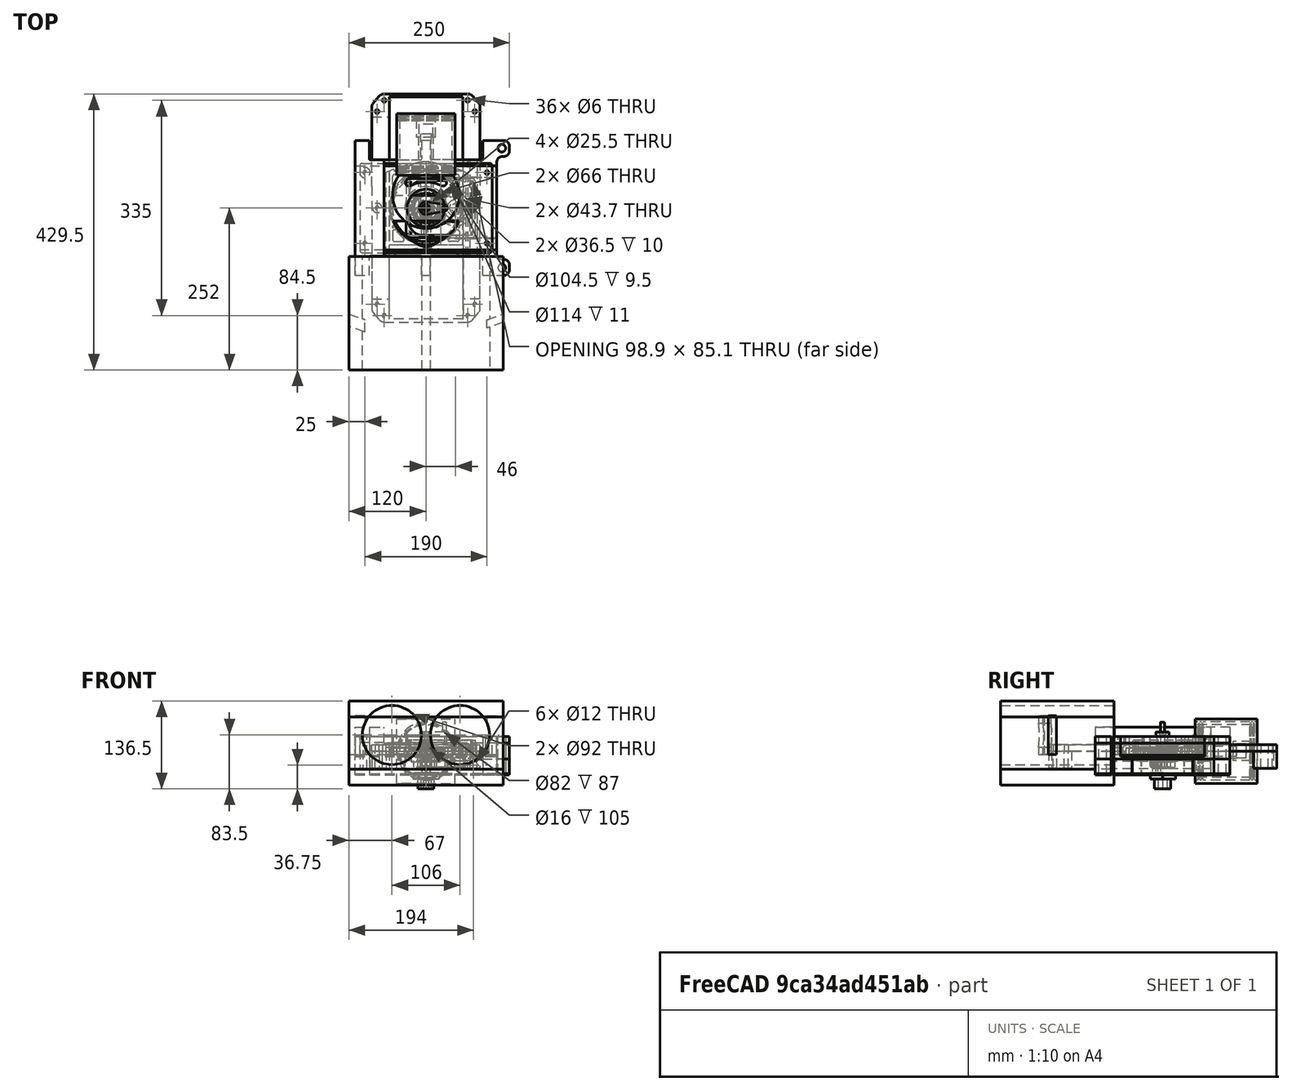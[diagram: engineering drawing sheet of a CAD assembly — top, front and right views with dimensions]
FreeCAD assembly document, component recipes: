
FREECAD ASSEMBLY — COMPONENT RECIPES ("assm4_Paired_at_Tusi_engine")

This assembly document has 39 components, labeled P0..P38 below (a component is one placed body or linked part). 38 of them carry a construction recipe — the FreeCAD feature program that regenerates the part from scratch, quoted from this document or its linked companion documents; the rest are supplied as boundary geometry only. No exploded tour is included for this assembly.
NOTE — this tour is split across 2 documents so each fits a 32k-token context. This is document 1: the component sections continue in the remaining 1 document, each repeating the header above.
COMPONENT P0 — geometry summary ("Assembly_total"; no construction recipe available for this part):
  bounding box: 108.1 x 92.0 x 62.2 mm
  tessellated surface: 9,740 triangles
  volume: 74990775681339383338264170385400035557474644223494673803599843481863248417572032395124455590544277504 mm^3 (12113090433333364260136632761595625055943688050167025185754855824423538995780718082348980511965184% of its bounding box)
  symmetry: mirror-symmetric across its x mid-plane
COMPONENT P1 — recipe-attached ("Шток_поршня", modeled in this document).
Construction recipe (the document's own serialized feature program — sketch geometry with constraints, then the solid features built on it; lengths are millimeters unless a unit is written):

FEATURE [PartDesign::CoordinateSystem] Pin
  AttacherType = Attacher::AttachEngine3D
  MapMode = 45
  Placement = pos=(5.1e-14,85,0) rot=(0.57735,0.57735,0.57735;2.0944rad)
FEATURE [Sketcher::SketchObject] Sketch053
  FullyConstrained = true
  MapMode = 5
  Placement = pos=(0,0,0) rot=(1,0,0;1.5708rad)
  Support = -> [XZ_Plane001]
  sketch-geometry (2):
    g0: Circle CenterX=0 CenterY=0 CenterZ=0 NormalX=0 NormalY=0 NormalZ=1 AngleXU=0 Radius=11
    g1: Circle CenterX=0 CenterY=0 CenterZ=0 NormalX=0 NormalY=0 NormalZ=1 AngleXU=0 Radius=8
  constraints (4):
    c: Coincident(g0,g-1)
    c: Coincident(g1,g0)
    c: Diameter(g0) = 22
    c: Diameter(g1) = 16
FEATURE [PartDesign::Pad] Pad
  Direction = (0,-1,-2e-16)
  Length = 115
  Length2 = 7.5
  Placement = pos=(0,0,0) rot=(1,0,0;1.5708rad)
  Profile = -> Sketch053
  ReferenceAxis = -> Sketch053 [N_Axis]
  Reversed = true
  Type = 4
FEATURE [Sketcher::SketchObject] Sketch054
  FullyConstrained = true
  MapMode = 5
  Placement = pos=(0,0,0) rot=(1,0,0;1.5708rad)
  Support = -> [XZ_Plane001]
  sketch-geometry (2):
    g0: Circle CenterX=0 CenterY=0 CenterZ=0 NormalX=0 NormalY=0 NormalZ=1 AngleXU=0 Radius=11
    g1: Circle CenterX=0 CenterY=0 CenterZ=0 NormalX=0 NormalY=0 NormalZ=1 AngleXU=0 Radius=3
  constraints (4):
    c: Coincident(g0,g-1)
    c: Diameter(g0) = 22
    c: Coincident(g1,g0)
    c: Diameter(g1) = 6
FEATURE [PartDesign::Pad] Pad025
  BaseFeature = -> Pad
  Direction = (0,-1,-2e-16)
  Length = 10
  Length2 = 10
  Placement = pos=(0,0,0) rot=(1,0,0;1.5708rad)
  Profile = -> Sketch054
  ReferenceAxis = -> Sketch054 [N_Axis]
  Reversed = true
  Type = 0
FEATURE [Sketcher::SketchObject] Sketch055
  ExternalGeometry = -> [Pad025]
  FullyConstrained = true
  MapMode = 5
  Placement = pos=(0,0,0) rot=(1,0,0;1.5708rad)
  Support = -> [XZ_Plane001]
  sketch-geometry (2):
    g0: Circle CenterX=0 CenterY=0 CenterZ=0 NormalX=0 NormalY=0 NormalZ=1 AngleXU=0 Radius=7
    g1: Circle CenterX=0 CenterY=0 CenterZ=0 NormalX=0 NormalY=0 NormalZ=1 AngleXU=0 Radius=3
  constraints (4):
    c: Coincident(g0,g-3)
    c: Diameter(g0) = 14
    c: Coincident(g1,g0)
    c: Equal(g-3,g1)
FEATURE [PartDesign::Pad] Pad026
  BaseFeature = -> Pad025
  Direction = (0,-1,-2e-16)
  Length = 45
  Length2 = 10
  Placement = pos=(0,0,0) rot=(1,0,0;1.5708rad)
  Profile = -> Sketch055
  ReferenceAxis = -> Sketch055 [N_Axis]
  Type = 0
FEATURE [PartDesign::Body] Body  label="Шток_поршня"
  Group = -> [Pin,Sketch053,Pad,Sketch054,Pad025,Sketch055,Pad026]
  Origin = -> Origin001
  Tip = -> Pad026
COMPONENT P2 — recipe-attached ("Эксцентрик", modeled in this document).
Construction recipe (the document's own serialized feature program — sketch geometry with constraints, then the solid features built on it; lengths are millimeters unless a unit is written):

FEATURE [Sketcher::SketchObject] Sketch005
  FullyConstrained = true
  MapMode = 5
  Support = -> [XY_Plane002]
  expr: Constraints[1] = <<Dim_table>>.crank_dia2 + <<Dim_table>>.zazor
  expr: Constraints[26] = <<Dim_table>>.crank_dia2 * 0.4
  expr: Constraints[27] = <<Dim_table>>.ecc_dia * 0.8
  expr: Constraints[29] = <<Dim_table>>.crank_dia2 * 1.5
  expr: Constraints[2] = <<Dim_table>>.ecc_dia
  expr: Constraints[3] = <<Dim_table>>.crank_len
  sketch-geometry (14):
    g0: Circle CenterX=0 CenterY=-9.5 CenterZ=0 NormalX=0 NormalY=0 NormalZ=1 AngleXU=0 Radius=18
    g1: Circle CenterX=0 CenterY=0 CenterZ=0 NormalX=0 NormalY=0 NormalZ=1 AngleXU=0 Radius=6.5
    g2: ArcOfCircle CenterX=0 CenterY=-9.5 CenterZ=0 NormalX=0 NormalY=0 NormalZ=1 AngleXU=0 Radius=14.4 StartAngle=2.38131 EndAngle=4.4845
    g3: ArcOfCircle CenterX=0 CenterY=-9.5 CenterZ=0 NormalX=0 NormalY=0 NormalZ=1 AngleXU=0 Radius=14.4 StartAngle=4.94028 EndAngle=7.04347
    g4: LineSegment StartX=-2.5 StartY=-9.49157 StartZ=0 EndX=-2.5 EndY=-22.9291 EndZ=0
    g5: LineSegment StartX=2.5 StartY=-9.49157 StartZ=0 EndX=2.5 EndY=-22.9291 EndZ=0
    g6: ArcOfCircle CenterX=0 CenterY=0 CenterZ=0 NormalX=0 NormalY=0 NormalZ=1 AngleXU=0 Radius=9.375 StartAngle=3.14159 EndAngle=4.39533
    g7: ArcOfCircle CenterX=0 CenterY=0 CenterZ=0 NormalX=0 NormalY=0 NormalZ=1 AngleXU=0 Radius=9.375 StartAngle=5.02945 EndAngle=6.28319
    g8: ArcOfCircle CenterX=-9.9895 CenterY=0 CenterZ=0 NormalX=0 NormalY=0 NormalZ=1 AngleXU=0 Radius=0.614498 StartAngle=0 EndAngle=2.38131
    g9: ArcOfCircle CenterX=9.9895 CenterY=0 CenterZ=0 NormalX=0 NormalY=0 NormalZ=1 AngleXU=0 Radius=0.614498 StartAngle=0.760287 EndAngle=3.14159
    g10: ArcOfCircle CenterX=-3.1145 CenterY=-22.9291 CenterZ=0 NormalX=0 NormalY=0 NormalZ=1 AngleXU=0 Radius=0.614498 StartAngle=4.4845 EndAngle=6.28319
    g11: ArcOfCircle CenterX=3.1145 CenterY=-22.9291 CenterZ=0 NormalX=0 NormalY=0 NormalZ=1 AngleXU=0 Radius=0.614498 StartAngle=3.14159 EndAngle=4.94028
    g12: ArcOfCircle CenterX=-3.1145 CenterY=-9.49157 CenterZ=0 NormalX=0 NormalY=0 NormalZ=1 AngleXU=0 Radius=0.614498 StartAngle=0 EndAngle=1.25373
    g13: ArcOfCircle CenterX=3.1145 CenterY=-9.49157 CenterZ=0 NormalX=0 NormalY=0 NormalZ=1 AngleXU=0 Radius=0.614498 StartAngle=1.88786 EndAngle=3.14159
  constraints (32):
    c: PointOnObject(g0,g-2)
    c: Diameter(g1) = 13
    c: Diameter(g0) = 36
    c: Distance(g1,g0) = 9.5
    c: Coincident(g1,g-1)
    c: Coincident(g2,g0)
    c: Coincident(g3,g0)
    c: Equal(g2,g3)
    c: Vertical(g4)
    c: Coincident(g6,g1)
    c: Coincident(g7,g1)
    c: Tangent(g2,g8) = -1.5708
    c: Tangent(g6,g8) = 1.5708
    c: Tangent(g7,g9) = 1.5708
    c: Tangent(g3,g9) = -1.5708
    c: Tangent(g2,g10) = -1.5708
    c: Tangent(g4,g10) = 1.5708
    c: Tangent(g5,g11) = -1.5708
    c: Tangent(g3,g11) = -1.5708
    c: Tangent(g6,g12) = 1.5708
    c: Tangent(g4,g12) = 1.5708
    c: Tangent(g5,g13) = -1.5708
    c: Tangent(g7,g13) = 1.5708
    c: Symmetric(g12,g13,g-2)
    c: Symmetric(g10,g11,g-2)
    c: Symmetric(g8,g9,g-2)
    c: DistanceX(g4,g5) = 5
    c: Diameter(g2) = 28.8
    c: PointOnObject(g8,g-1)
    c: Diameter(g6) = 18.75
    c: Equal(g12,g8)
    c: Equal(g10,g8)
FEATURE [PartDesign::CoordinateSystem] Eccentr
  AttacherType = Attacher::AttachEngine3D
  AttachmentOffset = pos=(0,0,0) rot=(0,0,1;1.5708rad)
  MapMode = 11
  Placement = pos=(0,0,0) rot=(0,0,1;3.14159rad)
  Support = -> [Sketch005]
FEATURE [PartDesign::Pad] Pad001
  Direction = (0,0,1)
  Length = 5.25
  Length2 = 5.25
  Profile = -> Sketch005
  ReferenceAxis = -> Sketch005 [N_Axis]
  Reversed = true
  Type = 4
  expr: Length = <<Dim_table>>.ecc_hei / 2 + <<Dim_table>>.zazor / 2
  expr: Length2 = <<Dim_table>>.ecc_hei / 2 + <<Dim_table>>.zazor / 2
FEATURE [PartDesign::Body] Body001  label="Эксцентрик"
  Group = -> [Sketch005,Pad001,Eccentr]
  Origin = -> Origin002
  Tip = -> Pad001
COMPONENT P3 — recipe-attached ("Ползун_рабочий", modeled in this document).
Construction recipe (the document's own serialized feature program — sketch geometry with constraints, then the solid features built on it; lengths are millimeters unless a unit is written):

FEATURE [Sketcher::SketchObject] Sketch007
  FullyConstrained = true
  MapMode = 5
  Support = -> [XY_Plane003]
  expr: Constraints[17] = <<Dim_table>>.ecc_dia * 1.25
  expr: Constraints[3] = <<Dim_table>>.ecc_dia + <<Dim_table>>.zazor
  expr: Constraints[4] = <<Dim_table>>.inter_shaft_len
  expr: Constraints[5] = <<Dim_table>>.inter_shaft_len / 2
  expr: Constraints[6] = <<Dim_table>>.piston_pin_dia
  expr: Constraints[7] = <<Dim_table>>.ecc_dia * 0.45
  sketch-geometry (8):
    g0: Circle CenterX=0 CenterY=0 CenterZ=0 NormalX=0 NormalY=0 NormalZ=1 AngleXU=0 Radius=18.25
    g1: Circle CenterX=46 CenterY=0 CenterZ=0 NormalX=0 NormalY=0 NormalZ=1 AngleXU=0 Radius=18.25
    g2: Circle CenterX=23 CenterY=16.2 CenterZ=0 NormalX=0 NormalY=0 NormalZ=1 AngleXU=0 Radius=2.5
    g3: Circle CenterX=23 CenterY=-16.2 CenterZ=0 NormalX=0 NormalY=0 NormalZ=1 AngleXU=0 Radius=2.5
    g4: ArcOfCircle CenterX=0 CenterY=0 CenterZ=0 NormalX=0 NormalY=0 NormalZ=1 AngleXU=0 Radius=22.5 StartAngle=1.5708 EndAngle=4.71239
    g5: ArcOfCircle CenterX=46 CenterY=0 CenterZ=0 NormalX=0 NormalY=0 NormalZ=1 AngleXU=0 Radius=22.5 StartAngle=4.71239 EndAngle=7.85398
    g6: LineSegment StartX=-3.6e-15 StartY=22.5 StartZ=0 EndX=46 EndY=22.5 EndZ=0
    g7: LineSegment StartX=-4.1e-15 StartY=-22.5 StartZ=0 EndX=46 EndY=-22.5 EndZ=0
  constraints (18):
    c: Coincident(g0,g-1)
    c: PointOnObject(g1,g-1)
    c: Equal(g0,g1)
    c: Diameter(g0) = 36.5
    c: DistanceX(g0,g1) = 46
    c: DistanceX(g-1,g2) = 23
    c: Diameter(g2) = 5
    c: DistanceY(g-1,g2) = 16.2
    c: Equal(g3,g2)
    c: Symmetric(g3,g2,g-1)
    c: Coincident(g4,g0)
    c: Equal(g4,g5)
    c: Tangent(g4,g7) = -1.5708
    c: Tangent(g7,g5) = -1.5708
    c: Tangent(g4,g6) = 1.5708
    c: Tangent(g6,g5) = 1.5708
    c: Coincident(g1,g5)
    c: Diameter(g4) = 45
FEATURE [PartDesign::Pad] Pad002
  Direction = (0,0,1)
  Length = 10
  Length2 = 10
  Midplane = true
  Profile = -> Sketch007
  ReferenceAxis = -> Sketch007 [N_Axis]
  Type = 0
  expr: Length = <<Dim_table>>.ecc_hei
FEATURE [PartDesign::CoordinateSystem] Shtok
  AttacherType = Attacher::AttachEngine3D
  MapMode = 45
  Placement = pos=(23,-1.5e-15,2e-16) rot=(0,0,1;1.5708rad)
  Support = -> [Pad002]
FEATURE [Sketcher::SketchObject] Sketch069
  ExternalGeometry = -> [Pad002]
  FullyConstrained = false
  MapMode = 5
  Support = -> [XY_Plane003]
  expr: Constraints[23] = <<Dim_table>>.piston_pin_dia * 2.5
  sketch-geometry (12):
    g0: LineSegment StartX=29.25 StartY=55.4001 StartZ=0 EndX=29.25 EndY=16.2 EndZ=0
    g1: LineSegment StartX=16.75 StartY=16.2 StartZ=0 EndX=16.75 EndY=45.3833 EndZ=0
    g2: ArcOfCircle CenterX=23 CenterY=16.2 CenterZ=0 NormalX=0 NormalY=0 NormalZ=1 AngleXU=0 Radius=6.25 StartAngle=3.14159 EndAngle=6.28319
    g3: LineSegment StartX=29.25 StartY=-53.7093 StartZ=0 EndX=29.25 EndY=-16.2 EndZ=0
    g4: LineSegment StartX=16.75 StartY=-16.2 StartZ=0 EndX=16.75 EndY=-45.7946 EndZ=0
    g5: ArcOfCircle CenterX=23 CenterY=-16.2 CenterZ=0 NormalX=0 NormalY=0 NormalZ=1 AngleXU=0 Radius=6.25 StartAngle=3.13e-14 EndAngle=3.14159
    g6: LineSegment StartX=16.75 StartY=45.3833 StartZ=0 EndX=-33.8127 EndY=45.3833 EndZ=0
    g7: LineSegment StartX=-33.8127 StartY=45.3833 StartZ=0 EndX=-33.8127 EndY=-45.7946 EndZ=0
    g8: LineSegment StartX=-33.8127 StartY=-45.7946 StartZ=0 EndX=16.75 EndY=-45.7946 EndZ=0
    g9: LineSegment StartX=29.25 StartY=-53.7093 StartZ=0 EndX=-45.8732 EndY=-53.7093 EndZ=0
    g10: LineSegment StartX=-45.8732 StartY=-53.7093 StartZ=0 EndX=-45.8732 EndY=55.4001 EndZ=0
    g11: LineSegment StartX=-45.8732 StartY=55.4001 StartZ=0 EndX=29.25 EndY=55.4001 EndZ=0
  constraints (26):
    c: Vertical(g0)
    c: Vertical(g1)
    c: Tangent(g2,g0) = 1.5708
    c: Tangent(g1,g2) = 1.5708
    c: Vertical(g3)
    c: Vertical(g4)
    c: Tangent(g5,g3) = -1.5708
    c: Tangent(g4,g5) = -1.5708
    c: Equal(g5,g2)
    c: Coincident(g1,g6)
    c: Horizontal(g6)
    c: Coincident(g6,g7)
    c: Vertical(g7)
    c: Coincident(g7,g8)
    c: Coincident(g8,g4)
    c: Horizontal(g8)
    c: Coincident(g3,g9)
    c: Horizontal(g9)
    c: Coincident(g9,g10)
    c: Vertical(g10)
    c: Coincident(g10,g11)
    c: Coincident(g11,g0)
    c: Horizontal(g11)
    c: Diameter(g2) = 12.5
    c: Coincident(g-3,g2)
    c: Coincident(g5,g-4)
FEATURE [PartDesign::Pocket] Pocket
  BaseFeature = -> Pad002
  Direction = (0,0,-1)
  Length = 5.5
  Length2 = 5
  Midplane = true
  Profile = -> Sketch069
  ReferenceAxis = -> Sketch069 [N_Axis]
  Type = 0
FEATURE [PartDesign::Chamfer] Chamfer
  Angle = 45
  Base = -> Pocket [Edge28,Edge27]
  BaseFeature = -> Pocket
  ChamferType = 0
  FlipDirection = false
  Size = 1
  Size2 = 1
  SupportTransform = false
  UseAllEdges = false
FEATURE [PartDesign::Body] Body002  label="Ползун_рабочий"
  Group = -> [Sketch007,Pad002,Shtok,Sketch069,Pocket,Chamfer]
  Origin = -> Origin003
  Tip = -> Chamfer
COMPONENT P4 — recipe-attached ("Шейка_шатунная", modeled in this document).
Construction recipe (the document's own serialized feature program — sketch geometry with constraints, then the solid features built on it; lengths are millimeters unless a unit is written):

FEATURE [Sketcher::SketchObject] Sketch004
  FullyConstrained = true
  MapMode = 5
  Support = -> [XY_Plane004]
  expr: Constraints[0] = <<Dim_table>>.crank_dia2
  expr: Constraints[2] = <<Dim_table>>.crank_len
  expr: Constraints[4] = <<Dim_table>>.axle_hole_dia
  sketch-geometry (2):
    g0: Circle CenterX=0 CenterY=-9.5 CenterZ=0 NormalX=0 NormalY=0 NormalZ=1 AngleXU=0 Radius=6.25
    g1: Circle CenterX=0 CenterY=-9.5 CenterZ=0 NormalX=0 NormalY=0 NormalZ=1 AngleXU=0 Radius=1.5
  constraints (5):
    c: Diameter(g0) = 12.5
    c: PointOnObject(g0,g-2)
    c: DistanceY(g0,g-1) = 9.5
    c: Coincident(g1,g0)
    c: Diameter(g1) = 3
FEATURE [PartDesign::Pad] Pad003
  Direction = (0,0,1)
  Length = 19
  Length2 = 0
  Profile = -> Sketch004
  ReferenceAxis = -> Sketch004 [N_Axis]
  Type = 0
FEATURE [Sketcher::SketchObject] Sketch070
  FullyConstrained = true
  MapMode = 11
  Placement = pos=(0,-9.5,19) rot=(0,0,1;1.5708rad)
  Support = -> [Pad003]
  expr: Constraints[12] = <<Dim_table>>.crank_dia2
  expr: Constraints[13] = <<Dim_table>>.axle_hole_dia
  expr: Constraints[14] = 0
  expr: Constraints[3] = <<Dim_table>>.crank_dia2 * 0.8
  sketch-geometry (5):
    g0: ArcOfCircle CenterX=0 CenterY=0 CenterZ=0 NormalX=0 NormalY=0 NormalZ=1 AngleXU=0 Radius=6.25 StartAngle=0.643501 EndAngle=2.49809
    g1: ArcOfCircle CenterX=0 CenterY=0 CenterZ=0 NormalX=0 NormalY=0 NormalZ=1 AngleXU=0 Radius=6.25 StartAngle=3.78509 EndAngle=5.63968
    g2: LineSegment StartX=5 StartY=3.75 StartZ=0 EndX=5 EndY=-3.75 EndZ=0
    g3: LineSegment StartX=-5 StartY=3.75 StartZ=0 EndX=-5 EndY=-3.75 EndZ=0
    g4: Circle CenterX=0 CenterY=0 CenterZ=0 NormalX=0 NormalY=0 NormalZ=1 AngleXU=0 Radius=1.5
  constraints (15):
    c: Coincident(g2,g0)
    c: Coincident(g2,g1)
    c: Vertical(g2)
    c: DistanceX(g0,g0) = 10
    c: Coincident(g3,g0)
    c: Coincident(g3,g1)
    c: Vertical(g3)
    c: Equal(g3,g2)
    c: Equal(g1,g0)
    c: Coincident(g1,g0)
    c: Coincident(g4,g0)
    c: PointOnObject(g0,g-2)
    c: Diameter(g0) = 12.5
    c: Diameter(g4) = 3
    c: DistanceY(g-1,g0) = 0
FEATURE [PartDesign::Pad] Pad038
  BaseFeature = -> Pad003
  Direction = (0,0,1)
  Length = 8
  Length2 = 10
  Profile = -> Sketch070
  ReferenceAxis = -> Sketch070 [N_Axis]
  TaperAngle = -2
  Type = 0
FEATURE [PartDesign::Body] Body003  label="Шейка_шатунная"
  Group = -> [Sketch004,Pad003,Sketch070,Pad038]
  Origin = -> Origin004
  Placement = pos=(0,0,-25) rot=(0,0,1;0rad)
  Tip = -> Pad038
COMPONENT P5 — recipe-attached ("Щека", modeled in this document).
Construction recipe (the document's own serialized feature program — sketch geometry with constraints, then the solid features built on it; lengths are millimeters unless a unit is written):

FEATURE [Sketcher::SketchObject] Sketch003
  FullyConstrained = true
  MapMode = 5
  Support = -> [XY_Plane005]
  expr: Constraints[17] = <<Dim_table>>.fillet_r
  expr: Constraints[18] = <<Dim_table>>.fillet_r
  expr: Constraints[21] = <<Dim_table>>.inter_shaft_len - <<Dim_table>>.zazor
  expr: Constraints[23] = <<Dim_table>>.axle_hole_dia
  expr: Constraints[24] = <<Inter_crank_gear01-1>>.root_diameter
  expr: Constraints[25] = 70
  expr: Constraints[26] = <<Dim_table>>.crank_dia2 * 1.5
  expr: Constraints[27] = <<Dim_table>>.crank_len
  sketch-geometry (14):
    g0: ArcOfCircle CenterX=0 CenterY=0 CenterZ=0 NormalX=0 NormalY=0 NormalZ=1 AngleXU=0 Radius=20.5 StartAngle=0.10832 EndAngle=3.03327
    g1: ArcOfCircle CenterX=3e-16 CenterY=-9.5 CenterZ=0 NormalX=0 NormalY=0 NormalZ=1 AngleXU=0 Radius=9.375 StartAngle=3.49066 EndAngle=5.93412
    g2: LineSegment StartX=-8.80962 StartY=-12.7064 StartZ=0 EndX=8.80962 EndY=-12.7064 EndZ=0
    g3: LineSegment StartX=-18.3916 StartY=0 StartZ=0 EndX=-14.8348 EndY=0 EndZ=0
    g4: LineSegment StartX=-12.9554 StartY=-1.31596 StartZ=0 EndX=-8.80962 EndY=-12.7064 EndZ=0
    g5: LineSegment StartX=8.80962 StartY=-12.7064 StartZ=0 EndX=12.9554 EndY=-1.31596 EndZ=0
    g6: LineSegment StartX=14.8348 StartY=4e-16 StartZ=0 EndX=18.3916 EndY=4e-16 EndZ=0
    g7: ArcOfCircle CenterX=-14.8348 CenterY=-2 CenterZ=0 NormalX=0 NormalY=0 NormalZ=1 AngleXU=0 Radius=2 StartAngle=0.349066 EndAngle=1.5708
    g8: ArcOfCircle CenterX=14.8348 CenterY=-2 CenterZ=0 NormalX=0 NormalY=0 NormalZ=1 AngleXU=0 Radius=2 StartAngle=1.5708 EndAngle=2.79253
    g9: ArcOfCircle CenterX=18.3916 CenterY=2 CenterZ=0 NormalX=0 NormalY=0 NormalZ=1 AngleXU=0 Radius=2 StartAngle=4.71239 EndAngle=6.39151
    g10: ArcOfCircle CenterX=-18.3916 CenterY=2 CenterZ=0 NormalX=0 NormalY=0 NormalZ=1 AngleXU=0 Radius=2 StartAngle=3.03327 EndAngle=4.71239
    g11: Circle CenterX=0 CenterY=0 CenterZ=0 NormalX=0 NormalY=0 NormalZ=1 AngleXU=0 Radius=22.75
    g12: Circle CenterX=0 CenterY=0 CenterZ=0 NormalX=0 NormalY=0 NormalZ=1 AngleXU=0 Radius=1.5
    g13: Circle CenterX=3e-16 CenterY=-9.5 CenterZ=0 NormalX=0 NormalY=0 NormalZ=1 AngleXU=0 Radius=1.5
  constraints (31):
    c: Coincident(g2,g1)
    c: Coincident(g2,g1)
    c: Horizontal(g2)
    c: Horizontal(g3)
    c: Horizontal(g6)
    c: Tangent(g4,g1) = -1.5708
    c: Tangent(g5,g1) = -1.5708
    c: Tangent(g3,g7) = 1.5708
    c: Tangent(g4,g7) = 1.5708
    c: Tangent(g6,g8) = 1.5708
    c: Tangent(g5,g8) = 1.5708
    c: Tangent(g6,g9) = -1.5708
    c: Tangent(g0,g9) = -1.5708
    c: Tangent(g0,g10) = -1.5708
    c: Tangent(g3,g10) = -1.5708
    c: Symmetric(g7,g8,g-2)
    c: Symmetric(g10,g9,g-2)
    c: Radius(g10) = 2
    c: Radius(g7) = 2
    c: Coincident(g0,g-1)
    c: Coincident(g11,g0)
    c: Diameter(g11) = 45.5
    c: Coincident(g12,g11)
    c: Diameter(g12) = 3
    c: Diameter(g0) = 41
    c: Angle(g5) = 1.22173
    c: Diameter(g1) = 18.75
    c: DistanceY(g1,g12) = 9.5
    c: PointOnObject(g3,g-1)
    c: Coincident(g13,g1)
    c: Equal(g13,g12)
FEATURE [PartDesign::Pad] Pad004
  Direction = (0,0,1)
  Length = 10
  Length2 = 10
  Profile = -> Sketch003
  ReferenceAxis = -> Sketch003 [N_Axis]
  Type = 0
FEATURE [PartDesign::Body] Body004  label="Щека"
  Group = -> [Sketch003,Pad004]
  Origin = -> Origin005
  Placement = pos=(0,0,12.5) rot=(0,0,1;0rad)
  Tip = -> Pad004
COMPONENT P6 — recipe-attached ("Шейка коренная", modeled in this document).
Construction recipe (the document's own serialized feature program — sketch geometry with constraints, then the solid features built on it; lengths are millimeters unless a unit is written):

FEATURE [Sketcher::SketchObject] Sketch002
  FullyConstrained = true
  MapMode = 5
  Support = -> [XY_Plane006]
  expr: Constraints[0] = <<Dim_table>>.crank_dia1
  expr: Constraints[20] = <<Dim_table>>.hex_size
  sketch-geometry (8):
    g0: Circle CenterX=0 CenterY=0 CenterZ=0 NormalX=0 NormalY=0 NormalZ=1 AngleXU=0 Radius=12.5
    g1: LineSegment StartX=4.04145 StartY=7 StartZ=0 EndX=-4.04145 EndY=7 EndZ=0
    g2: LineSegment StartX=-4.04145 StartY=7 StartZ=0 EndX=-8.0829 EndY=0 EndZ=0
    g3: LineSegment StartX=-8.0829 StartY=0 StartZ=0 EndX=-4.04145 EndY=-7 EndZ=0
    g4: LineSegment StartX=-4.04145 StartY=-7 StartZ=0 EndX=4.04145 EndY=-7 EndZ=0
    g5: LineSegment StartX=4.04145 StartY=-7 StartZ=0 EndX=8.0829 EndY=-9e-16 EndZ=0
    g6: LineSegment StartX=8.0829 StartY=-9e-16 StartZ=0 EndX=4.04145 EndY=7 EndZ=0
    g7: Circle CenterX=0 CenterY=0 CenterZ=0 NormalX=0 NormalY=0 NormalZ=1 AngleXU=0 Radius=8.0829
  constraints (18):
    c: Diameter(g0) = 25
    c: Coincident(g1,g2)
    c: Coincident(g2,g3)
    c: Coincident(g3,g4)
    c: Coincident(g4,g5)
    c: Coincident(g5,g6)
    c: Coincident(g6,g1)
    c: Equal(g1, g2-g6) x5
    c: PointOnObject(g1,g7)
    c: PointOnObject(g2,g7)
    c: PointOnObject(g3,g7)
    c: PointOnObject(g4,g7)
    c: PointOnObject(g5,g7)
    c: PointOnObject(g6,g7)
    c: Coincident(g7,g0)
    c: Horizontal(g1)
    c: DistanceY(g3,g1) = 14
    c: Coincident(g0,g-1)
FEATURE [PartDesign::Pad] Pad005
  Direction = (0,0,1)
  Length = 22.5
  Length2 = 10
  Profile = -> Sketch002
  ReferenceAxis = -> Sketch002 [N_Axis]
  Reversed = true
  Type = 0
FEATURE [PartDesign::Body] Body005  label="Шейка коренная"
  Group = -> [Sketch002,Pad005]
  Origin = -> Origin006
  Placement = pos=(0,0,47) rot=(0,0,1;0rad)
  Tip = -> Pad005
COMPONENT P7 — recipe-attached ("Body052", modeled in this document).
Construction recipe (the document's own serialized feature program — sketch geometry with constraints, then the solid features built on it; lengths are millimeters unless a unit is written):

FEATURE [PartDesign::FeatureBase] Clone002
  BaseFeature = -> Body003
FEATURE [PartDesign::Body] Body052
  Group = -> [Clone002]
  Origin = -> Origin053
  Placement = pos=(0,0,-35.5) rot=(0,0,1;0rad)
  Tip = -> Clone002
COMPONENT P8 — recipe-attached ("Body054", modeled in this document).
Construction recipe (the document's own serialized feature program — sketch geometry with constraints, then the solid features built on it; lengths are millimeters unless a unit is written):

FEATURE [PartDesign::FeatureBase] Clone004
  BaseFeature = -> Body005
FEATURE [PartDesign::Body] Body054
  Group = -> [Clone004]
  Origin = -> Origin055
  Placement = pos=(0,0,-36) rot=(0,0,1;0rad)
  Tip = -> Clone004
COMPONENT P9 — recipe-attached ("Body055", modeled in this document).
Construction recipe (the document's own serialized feature program — sketch geometry with constraints, then the solid features built on it; lengths are millimeters unless a unit is written):

FEATURE [PartDesign::FeatureBase] Clone005
  BaseFeature = -> Body004
FEATURE [PartDesign::Body] Body055
  Group = -> [Clone005]
  Origin = -> Origin056
  Placement = pos=(0,0,-43.5) rot=(0,0,1;0rad)
  Tip = -> Clone005
COMPONENT P10 — recipe-attached ("Колевал (секция)", modeled in this document).
Construction recipe (the document's own serialized feature program — sketch geometry with constraints, then the solid features built on it; lengths are millimeters unless a unit is written):

FEATURE [PartDesign::FeatureBase] Clone007
  BaseFeature = -> Fusion
FEATURE [PartDesign::CoordinateSystem] Crank_shaft
  AttacherType = Attacher::AttachEngine3D
  MapMode = 11
  Placement = pos=(0,0,-33.5) rot=(0,0,1;1.5708rad)
  Support = -> [Clone007]
FEATURE [PartDesign::Body] Body057  label="Колевал (секция)"
  Group = -> [Clone007,Crank_shaft]
  Origin = -> Origin058
  Tip = -> Clone007
COMPONENT P11 — recipe-attached ("Ползун_орто_новый", modeled in this document).
Construction recipe (the document's own serialized feature program — sketch geometry with constraints, then the solid features built on it; lengths are millimeters unless a unit is written):

FEATURE [Sketcher::SketchObject] Sketch018
  FullyConstrained = false
  expr: Constraints[0] = <<assm4_Main_BSM_M3_r80>>#<<Dim_table>>.ecc_dia + 0.5
  expr: Constraints[12] = <<assm4_Main_BSM_M3_r80>>#<<Dim_table>>.ecc_dia + 10
  sketch-geometry (34):
    g0: Circle CenterX=0 CenterY=0 CenterZ=0 NormalX=0 NormalY=0 NormalZ=1 AngleXU=0 Radius=52.25
    g1: LineSegment StartX=-57 StartY=-57 StartZ=0 EndX=57 EndY=-57 EndZ=0
    g2: LineSegment StartX=57 StartY=-57 StartZ=0 EndX=57 EndY=57 EndZ=0
    g3: LineSegment StartX=57 StartY=57 StartZ=0 EndX=-57 EndY=57 EndZ=0
    g4: LineSegment StartX=-57 StartY=57 StartZ=0 EndX=-57 EndY=-57 EndZ=0
    g5: LineSegment StartX=-57 StartY=57 StartZ=0 EndX=57 EndY=-57 EndZ=0
    g6: LineSegment StartX=-52.0662 StartY=36.8089 StartZ=0 EndX=-52.0662 EndY=48.6592 EndZ=0
    g7: LineSegment StartX=-48.6592 StartY=52.0662 StartZ=0 EndX=-36.8089 EndY=52.0662 EndZ=0
    g8: LineSegment StartX=-34.9598 StartY=47.602 StartZ=0 EndX=-47.602 EndY=34.9598 EndZ=0
    g9: ArcOfCircle CenterX=-48.6592 CenterY=48.6592 CenterZ=0 NormalX=0 NormalY=0 NormalZ=1 AngleXU=0 Radius=3.40698 StartAngle=1.5708 EndAngle=3.14159
    g10: ArcOfCircle CenterX=-36.8089 CenterY=49.4511 CenterZ=0 NormalX=0 NormalY=0 NormalZ=1 AngleXU=0 Radius=2.6151 StartAngle=5.49779 EndAngle=7.85398
    g11: ArcOfCircle CenterX=-49.4511 CenterY=36.8089 CenterZ=0 NormalX=0 NormalY=0 NormalZ=1 AngleXU=0 Radius=2.6151 StartAngle=3.14159 EndAngle=5.49779
    g12: LineSegment StartX=52.0638 StartY=36.7806 StartZ=0 EndX=52.0638 EndY=48.6568 EndZ=0
    g13: LineSegment StartX=48.6568 StartY=52.0638 StartZ=0 EndX=36.7806 EndY=52.0638 EndZ=0
    g14: LineSegment StartX=34.9329 StartY=47.603 StartZ=0 EndX=47.603 EndY=34.9329 EndZ=0
    g15: ArcOfCircle CenterX=48.6568 CenterY=48.6568 CenterZ=0 NormalX=0 NormalY=0 NormalZ=1 AngleXU=0 Radius=3.40698 StartAngle=0 EndAngle=1.5708
    g16: ArcOfCircle CenterX=36.7806 CenterY=49.4507 CenterZ=0 NormalX=0 NormalY=0 NormalZ=1 AngleXU=0 Radius=2.61303 StartAngle=1.5708 EndAngle=3.92699
    g17: ArcOfCircle CenterX=49.4507 CenterY=36.7806 CenterZ=0 NormalX=0 NormalY=0 NormalZ=1 AngleXU=0 Radius=2.61303 StartAngle=3.92699 EndAngle=6.28319
    g18: LineSegment StartX=-52.0638 StartY=-36.7806 StartZ=0 EndX=-52.0638 EndY=-48.6568 EndZ=0
    g19: LineSegment StartX=-48.6568 StartY=-52.0638 StartZ=0 EndX=-36.7806 EndY=-52.0638 EndZ=0
    g20: LineSegment StartX=-34.9329 StartY=-47.603 StartZ=0 EndX=-47.603 EndY=-34.9329 EndZ=0
    g21: ArcOfCircle CenterX=-48.6568 CenterY=-48.6568 CenterZ=0 NormalX=0 NormalY=0 NormalZ=1 AngleXU=0 Radius=3.40698 StartAngle=3.14159 EndAngle=4.71239
    g22: ArcOfCircle CenterX=-36.7806 CenterY=-49.4507 CenterZ=0 NormalX=0 NormalY=0 NormalZ=1 AngleXU=0 Radius=2.61303 StartAngle=4.71239 EndAngle=7.06858
    g23: ArcOfCircle CenterX=-49.4507 CenterY=-36.7806 CenterZ=0 NormalX=0 NormalY=0 NormalZ=1 AngleXU=0 Radius=2.61303 StartAngle=0.785398 EndAngle=3.14159
    g24: LineSegment StartX=52.0638 StartY=-36.7806 StartZ=0 EndX=52.0638 EndY=-48.6568 EndZ=0
    g25: LineSegment StartX=48.6568 StartY=-52.0638 StartZ=0 EndX=36.7806 EndY=-52.0638 EndZ=0
    g26: LineSegment StartX=34.9329 StartY=-47.603 StartZ=0 EndX=47.603 EndY=-34.9329 EndZ=0
    g27: ArcOfCircle CenterX=48.6568 CenterY=-48.6568 CenterZ=0 NormalX=0 NormalY=0 NormalZ=1 AngleXU=0 Radius=3.40698 StartAngle=4.71239 EndAngle=6.28319
    g28: ArcOfCircle CenterX=36.7806 CenterY=-49.4507 CenterZ=0 NormalX=0 NormalY=0 NormalZ=1 AngleXU=0 Radius=2.61303 StartAngle=2.35619 EndAngle=4.71239
    g29: ArcOfCircle CenterX=49.4507 CenterY=-36.7806 CenterZ=0 NormalX=0 NormalY=0 NormalZ=1 AngleXU=0 Radius=2.61303 StartAngle=0 EndAngle=2.35619
    g30: Circle CenterX=-51.4201 CenterY=29.3737 CenterZ=0 NormalX=0 NormalY=0 NormalZ=1 AngleXU=0 Radius=1.20268
    g31: Circle CenterX=51.4201 CenterY=29.3737 CenterZ=0 NormalX=0 NormalY=0 NormalZ=1 AngleXU=0 Radius=1.20268
    g32: Circle CenterX=-51.4201 CenterY=-29.3737 CenterZ=0 NormalX=0 NormalY=0 NormalZ=1 AngleXU=0 Radius=1.20268
    g33: Circle CenterX=51.4201 CenterY=-29.3737 CenterZ=0 NormalX=0 NormalY=0 NormalZ=1 AngleXU=0 Radius=1.20268
  constraints (52):
    c: Diameter(g0) = 104.5
    c: Coincident(g1,g2)
    c: Coincident(g2,g3)
    c: Coincident(g3,g4)
    c: Coincident(g4,g1)
    c: Horizontal(g3)
    c: Vertical(g2)
    c: Vertical(g4)
    c: Coincident(g5,g3)
    c: Coincident(g5,g1)
    c: Equal(g3,g4)
    c: Symmetric(g4,g2,g0)
    c: Distance(g2) = 114
    c: Coincident(g0,g-1)
    c: Horizontal(g1)
    c: Vertical(g6)
    c: Horizontal(g7)
    c: Equal(g6,g7)
    c: Tangent(g6,g9) = 1.5708
    c: Tangent(g7,g9) = 1.5708
    c: Tangent(g7,g10) = 1.5708
    c: Tangent(g8,g10) = 1.5708
    c: Tangent(g6,g11) = 1.5708
    c: Tangent(g8,g11) = 1.5708
    c: Symmetric(g11,g10,g5)
    c: Vertical(g12)
    c: Horizontal(g13)
    c: Equal(g12,g13)
    c: Tangent(g12,g15) = -1.5708
    c: Tangent(g13,g15) = -1.5708
    c: Tangent(g13,g16) = -1.5708
    c: Tangent(g14,g16) = -1.5708
    c: Tangent(g12,g17) = -1.5708
    c: Tangent(g14,g17) = -1.5708
    c: Vertical(g18)
    c: Horizontal(g19)
    c: Equal(g18,g19)
    c: Tangent(g18,g21) = -1.5708
    c: Tangent(g19,g21) = -1.5708
    c: Tangent(g19,g22) = -1.5708
    c: Tangent(g20,g22) = -1.5708
    c: Tangent(g18,g23) = -1.5708
    c: Tangent(g20,g23) = -1.5708
    c: Vertical(g24)
    c: Horizontal(g25)
    c: Equal(g24,g25)
    c: Tangent(g24,g27) = 1.5708
    c: Tangent(g25,g27) = 1.5708
    c: Tangent(g25,g28) = 1.5708
    c: Tangent(g26,g28) = 1.5708
    c: Tangent(g24,g29) = 1.5708
    c: Tangent(g26,g29) = 1.5708
FEATURE [PartDesign::Pad] Pad011
  Direction = (0,0,1)
  Length = 9.5
  Length2 = 10
  Midplane = true
  Profile = -> Sketch018
  ReferenceAxis = -> Sketch018 [N_Axis]
  Type = 0
FEATURE [Sketcher::SketchObject] Sketch
  ExternalGeometry = -> [Pad011]
  FullyConstrained = true
  MapMode = 5
  Placement = pos=(-57,0,0) rot=(0.57735,-0.57735,-0.57735;2.0944rad)
  Support = -> [Pad011]
  sketch-geometry (4):
    g0: ArcOfCircle CenterX=37.5722 CenterY=-1.24e-14 CenterZ=0 NormalX=0 NormalY=0 NormalZ=1 AngleXU=0 Radius=20 StartAngle=6.04339 EndAngle=6.52298
    g1: ArcOfCircle CenterX=-37.5722 CenterY=-1.14e-14 CenterZ=0 NormalX=0 NormalY=0 NormalZ=1 AngleXU=0 Radius=20 StartAngle=2.9018 EndAngle=3.38138
    g2: LineSegment StartX=-57 StartY=-4.75 StartZ=0 EndX=-57 EndY=4.75 EndZ=0
    g3: LineSegment StartX=57 StartY=-4.75 StartZ=0 EndX=57 EndY=4.75 EndZ=0
  constraints (10):
    c: Coincident(g0,g-3)
    c: Coincident(g0,g-3)
    c: Coincident(g1,g-4)
    c: Coincident(g1,g-4)
    c: Equal(g1,g0)
    c: Radius(g0) = 20
    c: Coincident(g2,g1)
    c: Coincident(g2,g1)
    c: Coincident(g3,g0)
    c: Coincident(g3,g0)
FEATURE [PartDesign::Pad] Pad037
  BaseFeature = -> Pad011
  Direction = (-1,0,0)
  Length = 114
  Length2 = 10
  Profile = -> Sketch
  ReferenceAxis = -> Sketch [N_Axis]
  Reversed = true
  Type = 0
  expr: Length = <<assm4_Main_BSM_M3_r80>>#<<Dim_table>>.ecc_dia + 10
FEATURE [PartDesign::CoordinateSystem] Shtok001
  AttacherType = Attacher::AttachEngine3D
  MapMode = 1
  Placement = pos=(-57,-57,-4.75) rot=(1,0,0;0rad)
  Support = -> [Pad037]
FEATURE [PartDesign::Body] Body060  label="Ползун_орто_новый"
  Group = -> [Sketch018,Pad011,Shtok001,Sketch,Pad037]
  Origin = -> Origin061
  Tip = -> Pad037
COMPONENT P12 — recipe-attached ("перегородка", modeled in this document).
Construction recipe (the document's own serialized feature program — sketch geometry with constraints, then the solid features built on it; lengths are millimeters unless a unit is written):

FEATURE [Sketcher::SketchObject] Sketch021
  FullyConstrained = false
  MapMode = 5
  Support = -> [XY_Plane062]
  sketch-geometry (30):
    g0: LineSegment StartX=-110 StartY=225 StartZ=0 EndX=110 EndY=225 EndZ=0
    g1: LineSegment StartX=110 StartY=225 StartZ=0 EndX=110 EndY=-225 EndZ=0
    g2: LineSegment StartX=110 StartY=-225 StartZ=0 EndX=-110 EndY=-225 EndZ=0
    g3: LineSegment StartX=-110 StartY=-225 StartZ=0 EndX=-110 EndY=225 EndZ=0
    g4: LineSegment StartX=-110 StartY=225 StartZ=0 EndX=-110 EndY=105 EndZ=0
    g5: LineSegment StartX=-110 StartY=105 StartZ=0 EndX=110 EndY=105 EndZ=0
    g6: LineSegment StartX=110 StartY=105 StartZ=0 EndX=110 EndY=225 EndZ=0
    g7: LineSegment StartX=-110 StartY=-225 StartZ=0 EndX=-110 EndY=-105 EndZ=0
    g8: LineSegment StartX=-110 StartY=-105 StartZ=0 EndX=110 EndY=-105 EndZ=0
    g9: LineSegment StartX=110 StartY=-105 StartZ=0 EndX=110 EndY=-225 EndZ=0
    g10: LineSegment StartX=-110 StartY=-105 StartZ=0 EndX=-110 EndY=105 EndZ=0
    g11: LineSegment StartX=110 StartY=105 StartZ=0 EndX=-110 EndY=105 EndZ=0
    g12: Circle CenterX=0 CenterY=0 CenterZ=0 NormalX=0 NormalY=0 NormalZ=1 AngleXU=0 Radius=33
    g13: LineSegment StartX=-110 StartY=105 StartZ=0 EndX=-110 EndY=0 EndZ=0
    g14: LineSegment StartX=110 StartY=-105 StartZ=0 EndX=110 EndY=105 EndZ=0
    g15: LineSegment StartX=110 StartY=105 StartZ=0 EndX=120.902 EndY=105 EndZ=0
    g16: LineSegment StartX=130 StartY=95.9016 StartZ=0 EndX=130 EndY=89.0984 EndZ=0
    g17: LineSegment StartX=120.902 StartY=80 StartZ=0 EndX=119.098 EndY=80 EndZ=0
    g18: ArcOfCircle CenterX=120.902 CenterY=95.9016 CenterZ=0 NormalX=0 NormalY=0 NormalZ=1 AngleXU=0 Radius=9.09838 StartAngle=0 EndAngle=1.5708
    g19: ArcOfCircle CenterX=120.902 CenterY=89.0984 CenterZ=0 NormalX=0 NormalY=0 NormalZ=1 AngleXU=0 Radius=9.09838 StartAngle=4.71239 EndAngle=6.28319
    g20: LineSegment StartX=110 StartY=70.9016 StartZ=0 EndX=110 EndY=0 EndZ=0
    g21: ArcOfCircle CenterX=119.098 CenterY=70.9016 CenterZ=0 NormalX=0 NormalY=0 NormalZ=1 AngleXU=0 Radius=9.09838 StartAngle=1.5708 EndAngle=3.14159
    g22: LineSegment StartX=110 StartY=-105 StartZ=0 EndX=120.902 EndY=-105 EndZ=0
    g23: LineSegment StartX=130 StartY=-95.9016 StartZ=0 EndX=130 EndY=-89.0984 EndZ=0
    g24: LineSegment StartX=120.902 StartY=-80 StartZ=0 EndX=119.098 EndY=-80 EndZ=0
    g25: ArcOfCircle CenterX=120.902 CenterY=-95.9016 CenterZ=0 NormalX=0 NormalY=0 NormalZ=1 AngleXU=0 Radius=9.09838 StartAngle=4.71239 EndAngle=6.28319
    g26: ArcOfCircle CenterX=120.902 CenterY=-89.0984 CenterZ=0 NormalX=0 NormalY=0 NormalZ=1 AngleXU=0 Radius=9.09838 StartAngle=0 EndAngle=1.5708
    g27: LineSegment StartX=110 StartY=-70.9016 StartZ=0 EndX=110 EndY=0 EndZ=0
    g28: ArcOfCircle CenterX=119.098 CenterY=-70.9016 CenterZ=0 NormalX=0 NormalY=0 NormalZ=1 AngleXU=0 Radius=9.09838 StartAngle=3.14159 EndAngle=4.71239
    g29: LineSegment StartX=-110 StartY=-105 StartZ=0 EndX=-110 EndY=0 EndZ=0
  constraints (61):
    c: Coincident(g0,g1)
    c: Coincident(g1,g2)
    c: Coincident(g2,g3)
    c: Coincident(g3,g0)
    c: Horizontal(g2)
    c: Vertical(g1)
    c: Symmetric(g0,g0,g-2)
    c: Symmetric(g0,g2,g-1)
    c: Coincident(g0,g4)
    c: PointOnObject(g4,g3)
    c: Coincident(g4,g5)
    c: PointOnObject(g5,g1)
    c: Horizontal(g5)
    c: Coincident(g6,g0)
    c: Coincident(g2,g7)
    c: PointOnObject(g7,g3)
    c: Horizontal(g8)
    c: Coincident(g9,g2)
    c: Equal(g9,g6)
    c: DistanceX(g2,g2) = 220
    c: DistanceY(g3,g3) = 450
    c: DistanceY(g9,g9) = 120
    c: Coincident(g10,g4)
    c: Coincident(g11,g10)
    c: Diameter(g12) = 66
    c: PointOnObject(g13,g-1)
    c: Vertical(g13)
    c: Vertical(g10)
    c: Vertical(g6)
    c: Coincident(g8,g9)
    c: Coincident(g8,g7)
    c: Coincident(g11,g5)
    c: Symmetric(g8,g11,g-1)
    c: Horizontal(g15)
    c: Horizontal(g17)
    c: Vertical(g16)
    c: Tangent(g15,g18) = 1.5708
    c: Tangent(g16,g18) = 1.5708
    c: Tangent(g16,g19) = 1.5708
    c: Tangent(g17,g19) = 1.5708
    c: Equal(g19,g18)
    c: Vertical(g20)
    c: Tangent(g17,g21) = -1.5708
    c: Tangent(g20,g21) = -1.5708
    c: Equal(g19,g21)
    c: Vertical(g14)
    c: Horizontal(g22)
    c: Horizontal(g24)
    c: Vertical(g23)
    c: Tangent(g22,g25) = -1.5708
    c: Tangent(g23,g25) = -1.5708
    c: Tangent(g23,g26) = -1.5708
    c: Tangent(g24,g26) = -1.5708
    c: Equal(g26,g25)
    c: Vertical(g27)
    c: Tangent(g24,g28) = 1.5708
    c: Tangent(g27,g28) = 1.5708
    c: Equal(g26,g28)
    c: Coincident(g13,g11)
    c: Coincident(g29,g8)
    c: Coincident(g29,g13)
FEATURE [Sketcher::SketchObject] Sketch022
  FullyConstrained = true
  MapMode = 5
  Support = -> [XY_Plane062]
  sketch-geometry (5):
    g0: LineSegment StartX=-110 StartY=-105 StartZ=0 EndX=-65.5 EndY=-105 EndZ=0
    g1: LineSegment StartX=-65.5 StartY=-105 StartZ=0 EndX=-65.5 EndY=105 EndZ=0
    g2: LineSegment StartX=-65.5 StartY=105 StartZ=0 EndX=-110 EndY=105 EndZ=0
    g3: LineSegment StartX=-110 StartY=105 StartZ=0 EndX=-110 EndY=-105 EndZ=0
    g4: LineSegment StartX=65.5 StartY=52.9337 StartZ=0 EndX=65.5 EndY=105 EndZ=0
  constraints (14):
    c: Coincident(g0,g1)
    c: Coincident(g1,g2)
    c: Coincident(g2,g3)
    c: Coincident(g3,g0)
    c: Horizontal(g0)
    c: Horizontal(g2)
    c: Vertical(g3)
    c: Vertical(g4)
    c: DistanceX(g1,g4) = 131
    c: Symmetric(g1,g4,g-2)
    c: DistanceY(g1,g1) = 210
    c: DistanceX(g0,g0) = 44.5
    c: Symmetric(g0,g1,g-1)
    c: Block(g4)
FEATURE [PartDesign::Pad] Pad012
  Direction = (0,0,1)
  Length = 35
  Length2 = 12.5
  Profile = -> Sketch021
  ReferenceAxis = -> Sketch021 [N_Axis]
  Reversed = true
  Type = 4
FEATURE [PartDesign::Pad] Pad013
  BaseFeature = -> Pad012
  Direction = (0,0,1)
  Length = 37.5
  Length2 = -12.5
  Profile = -> Sketch022
  ReferenceAxis = -> Sketch022 [N_Axis]
  Type = 4
FEATURE [Sketcher::SketchObject] Sketch_1
  FullyConstrained = false
  sketch-geometry (8):
    g0: Circle CenterX=0 CenterY=0 CenterZ=0 NormalX=0 NormalY=0 NormalZ=1 AngleXU=0 Radius=65.5
    g1: ArcOfCircle CenterX=0 CenterY=0 CenterZ=0 NormalX=0 NormalY=0 NormalZ=1 AngleXU=0 Radius=65.5 StartAngle=1.5708 EndAngle=4.71239
    g2: LineSegment StartX=145.598 StartY=65.5 StartZ=0 EndX=0 EndY=65.5 EndZ=0
    g3: LineSegment StartX=145.598 StartY=-65.5 StartZ=0 EndX=0 EndY=-65.5 EndZ=0
    g4: LineSegment StartX=145.598 StartY=65.5 StartZ=0 EndX=145.598 EndY=-65.5 EndZ=0
    g5: LineSegment StartX=-153.016 StartY=65.5 StartZ=0 EndX=0 EndY=65.5 EndZ=0
    g6: LineSegment StartX=-1.2e-14 StartY=-65.5 StartZ=0 EndX=-153.016 EndY=-65.5 EndZ=0
    g7: LineSegment StartX=-153.016 StartY=-65.5 StartZ=0 EndX=-153.016 EndY=65.5 EndZ=0
  constraints (18):
    c: Coincident(g0,g-1)
    c: Diameter(g0) = 131
    c: Coincident(g1,g0)
    c: PointOnObject(g1,g0)
    c: Horizontal(g2)
    c: Horizontal(g3)
    c: Tangent(g3,g1) = 1.5708
    c: Tangent(g1,g2) = -1.5708
    c: Coincident(g4,g2)
    c: Coincident(g4,g3)
    c: Vertical(g4)
    c: Coincident(g6,g7)
    c: Coincident(g7,g5)
    c: Horizontal(g5)
    c: Horizontal(g6)
    c: Vertical(g7)
    c: Coincident(g5,g2)
    c: Coincident(g6,g3)
FEATURE [PartDesign::Pocket] Pocket005
  BaseFeature = -> Pad013
  Direction = (0,0,-1)
  Length = 6.5
  Length2 = 13
  Profile = -> Sketch_1
  ReferenceAxis = -> Sketch_1 [N_Axis]
  Type = 4
FEATURE [PartDesign::CoordinateSystem] Block_ribb
  AttacherType = Attacher::AttachEngine3D
  MapMode = 2
  Support = -> [Pocket005]
FEATURE [Sketcher::SketchObject] Sketch_2
  FullyConstrained = false
  sketch-geometry (44):
    g0: LineSegment StartX=-0.25 StartY=33.6074 StartZ=0 EndX=-0.25 EndY=47.5 EndZ=0
    g1: LineSegment StartX=-0.25 StartY=47.5 StartZ=0 EndX=126.736 EndY=47.5 EndZ=0
    g2: LineSegment StartX=126.736 StartY=47.5 StartZ=0 EndX=126.736 EndY=47 EndZ=0
    g3: LineSegment StartX=126.736 StartY=47 StartZ=0 EndX=0.25 EndY=47 EndZ=0
    g4: LineSegment StartX=0.25 StartY=47 StartZ=0 EndX=0.25 EndY=33.6074 EndZ=0
    g5: LineSegment StartX=0.25 StartY=33.6074 StartZ=0 EndX=-0.25 EndY=33.6074 EndZ=0
    g6: ArcOfCircle CenterX=86.75 CenterY=76.5 CenterZ=0 NormalX=0 NormalY=0 NormalZ=1 AngleXU=0 Radius=1.5 StartAngle=4.71239 EndAngle=6.28319
    g7: ArcOfCircle CenterX=8.25 CenterY=76.5 CenterZ=0 NormalX=0 NormalY=0 NormalZ=1 AngleXU=0 Radius=1.5 StartAngle=3.14159 EndAngle=4.71239
    g8: LineSegment StartX=86.75 StartY=75 StartZ=0 EndX=8.25 EndY=75 EndZ=0
    g9: LineSegment StartX=88.25 StartY=105 StartZ=0 EndX=6.75 EndY=105 EndZ=0
    g10: LineSegment StartX=6.75 StartY=105 StartZ=0 EndX=6.75 EndY=76.5 EndZ=0
    g11: LineSegment StartX=88.25 StartY=105 StartZ=0 EndX=88.25 EndY=76.5 EndZ=0
    g12: GeomPoint X=47.5 Y=105 Z=0
    g13: Circle CenterX=-118 CenterY=93 CenterZ=0 NormalX=0 NormalY=0 NormalZ=1 AngleXU=0 Radius=6
    g14: Circle CenterX=118 CenterY=93 CenterZ=0 NormalX=0 NormalY=0 NormalZ=1 AngleXU=0 Radius=6
    g15: LineSegment StartX=-0.067348 StartY=-33.6074 StartZ=0 EndX=-0.067348 EndY=-47.5 EndZ=0
    g16: LineSegment StartX=-0.067348 StartY=-47.5 StartZ=0 EndX=126.736 EndY=-47.5 EndZ=0
    g17: LineSegment StartX=126.736 StartY=-47.5 StartZ=0 EndX=126.736 EndY=-47 EndZ=0
    g18: LineSegment StartX=126.736 StartY=-47 StartZ=0 EndX=0.25 EndY=-47 EndZ=0
    g19: LineSegment StartX=0.25 StartY=-47 StartZ=0 EndX=0.25 EndY=-33.6074 EndZ=0
    g20: LineSegment StartX=0.25 StartY=-33.6074 StartZ=0 EndX=-0.067348 EndY=-33.6074 EndZ=0
    g21: ArcOfCircle CenterX=-86.75 CenterY=76.5 CenterZ=0 NormalX=0 NormalY=0 NormalZ=1 AngleXU=0 Radius=1.5 StartAngle=3.14159 EndAngle=4.71239
    g22: ArcOfCircle CenterX=-8.25 CenterY=76.5 CenterZ=0 NormalX=0 NormalY=0 NormalZ=1 AngleXU=0 Radius=1.5 StartAngle=4.71239 EndAngle=6.28319
    g23: LineSegment StartX=-86.75 StartY=75 StartZ=0 EndX=-8.25 EndY=75 EndZ=0
    g24: LineSegment StartX=-88.25 StartY=105 StartZ=0 EndX=-6.75 EndY=105 EndZ=0
    g25: LineSegment StartX=-6.75 StartY=105 StartZ=0 EndX=-6.75 EndY=76.5 EndZ=0
    g26: LineSegment StartX=-88.25 StartY=105 StartZ=0 EndX=-88.25 EndY=76.5 EndZ=0
    g27: GeomPoint X=-47.5 Y=105 Z=0
    g28: ArcOfCircle CenterX=86.75 CenterY=-76.5 CenterZ=0 NormalX=0 NormalY=0 NormalZ=1 AngleXU=0 Radius=1.5 StartAngle=0 EndAngle=1.5708
    g29: ArcOfCircle CenterX=8.25 CenterY=-76.5 CenterZ=0 NormalX=0 NormalY=0 NormalZ=1 AngleXU=0 Radius=1.5 StartAngle=1.5708 EndAngle=3.14159
    g30: LineSegment StartX=86.75 StartY=-75 StartZ=0 EndX=8.25 EndY=-75 EndZ=0
    g31: LineSegment StartX=88.25 StartY=-105 StartZ=0 EndX=6.75 EndY=-105 EndZ=0
    g32: LineSegment StartX=6.75 StartY=-105 StartZ=0 EndX=6.75 EndY=-76.5 EndZ=0
    g33: LineSegment StartX=88.25 StartY=-105 StartZ=0 EndX=88.25 EndY=-76.5 EndZ=0
    g34: GeomPoint X=47.5 Y=-105 Z=0
    g35: Circle CenterX=-118 CenterY=-93 CenterZ=0 NormalX=0 NormalY=0 NormalZ=1 AngleXU=0 Radius=6
    g36: Circle CenterX=118 CenterY=-93 CenterZ=0 NormalX=0 NormalY=0 NormalZ=1 AngleXU=0 Radius=6
    g37: ArcOfCircle CenterX=-86.75 CenterY=-76.5 CenterZ=0 NormalX=0 NormalY=0 NormalZ=1 AngleXU=0 Radius=1.5 StartAngle=1.5708 EndAngle=3.14159
    g38: ArcOfCircle CenterX=-8.25 CenterY=-76.5 CenterZ=0 NormalX=0 NormalY=0 NormalZ=1 AngleXU=0 Radius=1.5 StartAngle=0 EndAngle=1.5708
    g39: LineSegment StartX=-86.75 StartY=-75 StartZ=0 EndX=-8.25 EndY=-75 EndZ=0
    g40: LineSegment StartX=-88.25 StartY=-105 StartZ=0 EndX=-6.75 EndY=-105 EndZ=0
    g41: LineSegment StartX=-6.75 StartY=-105 StartZ=0 EndX=-6.75 EndY=-76.5 EndZ=0
    g42: LineSegment StartX=-88.25 StartY=-105 StartZ=0 EndX=-88.25 EndY=-76.5 EndZ=0
    g43: GeomPoint X=-47.5 Y=-105 Z=0
  constraints (95):
    c: Vertical(g0)
    c: Coincident(g0,g1)
    c: Horizontal(g1)
    c: Coincident(g1,g2)
    c: Coincident(g2,g3)
    c: Horizontal(g3)
    c: Coincident(g3,g4)
    c: Vertical(g4)
    c: Coincident(g4,g5)
    c: Coincident(g5,g0)
    c: Vertical(g2)
    c: DistanceY(g2,g2) = 0.5
    c: DistanceX(g5,g5) = 0.5
    c: Tangent(g6,g8) = 1.5708
    c: Tangent(g8,g7) = 1.5708
    c: Equal(g6,g7)
    c: Horizontal(g8)
    c: Horizontal(g9)
    c: Vertical(g11)
    c: Vertical(g10)
    c: Tangent(g6,g11) = 1.5708
    c: Tangent(g7,g10) = -1.5708
    c: Coincident(g11,g9)
    c: Coincident(g9,g10)
    c: Symmetric(g9,g9,g12)
    c: Radius(g7) = 1.5
    c: Distance(g7,g9) = 30
    c: Diameter(g13) = 12
    c: Symmetric(g0,g4,g-2)
    c: DistanceY(g-1,g13) = 93
    c: DistanceX(g13,g-1) = 118
    c: DistanceY(g-1,g9) = 105
    c: DistanceX(g9,g9) = 81.5
    c: DistanceX(g-1,g9) = 6.75
    c: Diameter(g14) = 12
    c: Vertical(g15)
    c: Coincident(g15,g16)
    c: Horizontal(g16)
    c: Coincident(g16,g17)
    c: Coincident(g17,g18)
    c: Horizontal(g18)
    c: Coincident(g18,g19)
    c: Vertical(g19)
    c: Coincident(g19,g20)
    c: Coincident(g20,g15)
    c: Vertical(g17)
    c: Tangent(g21,g23) = -1.5708
    c: Tangent(g23,g22) = -1.5708
    c: Equal(g21,g22)
    c: Horizontal(g23)
    c: Horizontal(g24)
    c: Vertical(g26)
    c: Vertical(g25)
    c: Tangent(g21,g26) = -1.5708
    c: Tangent(g22,g25) = 1.5708
    c: Coincident(g26,g24)
    c: Coincident(g24,g25)
    c: Symmetric(g24,g24,g27)
    c: Radius(g22) = 1.5
    c: Distance(g22,g24) = 30
    c: Tangent(g28,g30) = -1.5708
    c: Tangent(g30,g29) = -1.5708
    c: Equal(g28,g29)
    c: Horizontal(g30)
    c: Horizontal(g31)
    c: Vertical(g33)
    c: Vertical(g32)
    c: Tangent(g28,g33) = -1.5708
    c: Tangent(g29,g32) = 1.5708
    c: Coincident(g33,g31)
    c: Coincident(g31,g32)
    c: Symmetric(g31,g31,g34)
    c: Radius(g29) = 1.5
    c: Distance(g29,g31) = 30
    c: Diameter(g35) = 12
    c: Diameter(g36) = 12
    c: Tangent(g37,g39) = 1.5708
    c: Tangent(g39,g38) = 1.5708
    c: Equal(g37,g38)
    c: Horizontal(g39)
    c: Horizontal(g40)
    c: Vertical(g42)
    c: Vertical(g41)
    c: Tangent(g37,g42) = 1.5708
    c: Tangent(g38,g41) = -1.5708
    c: Coincident(g42,g40)
    c: Coincident(g40,g41)
    c: Symmetric(g40,g40,g43)
    c: Radius(g38) = 1.5
    c: Distance(g38,g40) = 30
    c: Symmetric(g19,g4,g-1)
    c: Horizontal(g20)
    c: Symmetric(g17,g2,g-1)
    c: DistanceY(g17,g17) = 0.5
    c: DistanceY(g16,g1) = 95
FEATURE [PartDesign::Pocket] Pocket006
  BaseFeature = -> Pocket005
  Direction = (0,0,-1)
  Length = 50
  Length2 = 50
  Profile = -> Sketch_2
  ReferenceAxis = -> Sketch_2 [N_Axis]
  Type = 4
FEATURE [Sketcher::SketchObject] Sketch028
  FullyConstrained = true
  MapMode = 5
  Placement = pos=(0,-75,0) rot=(1,0,0;1.5708rad)
  sketch-geometry (1):
    g0: Circle CenterX=74 CenterY=-21.75 CenterZ=0 NormalX=0 NormalY=0 NormalZ=1 AngleXU=0 Radius=6
  constraints (3):
    c: Diameter(g0) = 12
    c: DistanceY(g0,g-1) = 21.75
    c: DistanceX(g-1,g0) = 74
FEATURE [PartDesign::Pocket] Pocket011
  BaseFeature = -> Pocket006
  Direction = (0,1,-2e-16)
  Length = 5
  Length2 = 5
  Profile = -> Sketch028
  ReferenceAxis = -> Sketch028 [N_Axis]
  Type = 1
FEATURE [PartDesign::Body] Body061  label="перегородка"
  Group = -> [Sketch022,Sketch021,Pad012,Pad013,Sketch_1,Pocket005,Block_ribb,Sketch_2,Pocket006,Sketch028,Pocket011]
  Origin = -> Origin062
  Tip = -> Pocket011
COMPONENT P13 — recipe-attached ("Перегородка_передняя", modeled in this document).
Construction recipe (the document's own serialized feature program — sketch geometry with constraints, then the solid features built on it; lengths are millimeters unless a unit is written):

FEATURE [PartDesign::Pad] Pad017
  Direction = (0,0,1)
  Length = 37
  Length2 = 22.5
  Profile = -> Sketch021
  ReferenceAxis = -> Sketch021 [N_Axis]
  Reversed = true
  Type = 4
FEATURE [PartDesign::Pocket] Pocket017
  BaseFeature = -> Pad017
  Direction = (0,0,-1)
  Length = 8.5
  Length2 = 13
  Profile = -> Sketch_1
  ReferenceAxis = -> Sketch_1 [N_Axis]
  Type = 4
FEATURE [PartDesign::CoordinateSystem] Block_ribb001
  AttacherType = Attacher::AttachEngine3D
  MapMode = 2
  Support = -> [Pocket017]
FEATURE [PartDesign::Pocket] Pocket018
  BaseFeature = -> Pocket017
  Direction = (0,0,-1)
  Length = 50
  Length2 = 50
  Profile = -> Sketch_2
  ReferenceAxis = -> Sketch_2 [N_Axis]
  Type = 4
FEATURE [PartDesign::Pocket] Pocket019
  BaseFeature = -> Pocket018
  Direction = (0,1,-2e-16)
  Length = 5
  Length2 = 5
  Profile = -> Sketch028
  ReferenceAxis = -> Sketch028 [N_Axis]
  Type = 1
FEATURE [Sketcher::SketchObject] Sketch034
  FullyConstrained = false
  MapMode = 5
  Support = -> [XY_Plane062]
  sketch-geometry (4):
    g0: LineSegment StartX=-154.224 StartY=65.5 StartZ=0 EndX=161.628 EndY=65.5 EndZ=0
    g1: LineSegment StartX=161.628 StartY=65.5 StartZ=0 EndX=161.628 EndY=-65.5 EndZ=0
    g2: LineSegment StartX=161.628 StartY=-65.5 StartZ=0 EndX=-154.224 EndY=-65.5 EndZ=0
    g3: LineSegment StartX=-154.224 StartY=-65.5 StartZ=0 EndX=-154.224 EndY=65.5 EndZ=0
  constraints (9):
    c: Coincident(g0,g1)
    c: Coincident(g1,g2)
    c: Coincident(g2,g3)
    c: Coincident(g3,g0)
    c: Horizontal(g0)
    c: Horizontal(g2)
    c: Vertical(g3)
    c: Symmetric(g1,g0,g-1)
    c: DistanceY(g1,g1) = 131
FEATURE [PartDesign::Pocket] Pocket020
  BaseFeature = -> Pocket019
  Direction = (0,0,-1)
  Length = 25
  Length2 = -10.5
  Profile = -> Sketch034
  ReferenceAxis = -> Sketch034 [N_Axis]
  Reversed = true
  Type = 4
FEATURE [PartDesign::Body] Body063  label="Перегородка_передняя"
  Group = -> [Pad017,Pocket017,Block_ribb001,Pocket018,Pocket019,Sketch034,Pocket020]
  Origin = -> Origin064
  Tip = -> Pocket020
COMPONENT P14 — recipe-attached ("перегородка_ползуна", modeled in this document).
Construction recipe (the document's own serialized feature program — sketch geometry with constraints, then the solid features built on it; lengths are millimeters unless a unit is written):

FEATURE [PartDesign::CoordinateSystem] Block_ribb002
  AttacherType = Attacher::AttachEngine3D
  MapMode = 2
FEATURE [PartDesign::Pad] Pad018
  Direction = (0,0,1)
  Length = 12.5
  Length2 = 12.5
  Profile = -> Sketch021
  ReferenceAxis = -> Sketch021 [N_Axis]
  Reversed = true
  Type = 4
FEATURE [Sketcher::SketchObject] Sketch035
  FullyConstrained = false
  MapMode = 5
  sketch-geometry (9):
    g0: LineSegment StartX=-110 StartY=-105 StartZ=0 EndX=-65.5 EndY=-105 EndZ=0
    g1: LineSegment StartX=-65.5 StartY=-105 StartZ=0 EndX=-65.5 EndY=105 EndZ=0
    g2: LineSegment StartX=-65.5 StartY=105 StartZ=0 EndX=-110 EndY=105 EndZ=0
    g3: LineSegment StartX=-110 StartY=105 StartZ=0 EndX=-110 EndY=-105 EndZ=0
    g4: LineSegment StartX=65.5 StartY=52.7372 StartZ=0 EndX=65.5 EndY=105 EndZ=0
    g5: LineSegment StartX=-110 StartY=-105 StartZ=0 EndX=65.5 EndY=-105 EndZ=0
    g6: LineSegment StartX=65.5 StartY=-105 StartZ=0 EndX=65.5 EndY=105 EndZ=0
    g7: LineSegment StartX=65.5 StartY=105 StartZ=0 EndX=-110 EndY=105 EndZ=0
    g8: LineSegment StartX=-110 StartY=105 StartZ=0 EndX=-110 EndY=-105 EndZ=0
  constraints (23):
    c: Coincident(g0,g1)
    c: Coincident(g1,g2)
    c: Coincident(g2,g3)
    c: Coincident(g3,g0)
    c: Horizontal(g0)
    c: Horizontal(g2)
    c: Vertical(g3)
    c: Vertical(g4)
    c: DistanceX(g1,g4) = 131
    c: Symmetric(g1,g4,g-2)
    c: DistanceY(g1,g1) = 210
    c: DistanceX(g0,g0) = 44.5
    c: Symmetric(g0,g1,g-1)
    c: Coincident(g5,g6)
    c: Coincident(g6,g7)
    c: Coincident(g7,g8)
    c: Coincident(g8,g5)
    c: Horizontal(g5)
    c: Horizontal(g7)
    c: Vertical(g6)
    c: Vertical(g8)
    c: Coincident(g5,g0)
    c: Coincident(g6,g4)
FEATURE [Sketcher::SketchObject] Sketch_004
  FullyConstrained = false
  sketch-geometry (32):
    g0: ArcOfCircle CenterX=86.75 CenterY=76.5 CenterZ=0 NormalX=0 NormalY=0 NormalZ=1 AngleXU=0 Radius=1.5 StartAngle=4.71239 EndAngle=6.28319
    g1: ArcOfCircle CenterX=8.25 CenterY=76.5 CenterZ=0 NormalX=0 NormalY=0 NormalZ=1 AngleXU=0 Radius=1.5 StartAngle=3.14159 EndAngle=4.71239
    g2: LineSegment StartX=86.75 StartY=75 StartZ=0 EndX=8.25 EndY=75 EndZ=0
    g3: LineSegment StartX=88.25 StartY=105 StartZ=0 EndX=6.75 EndY=105 EndZ=0
    g4: LineSegment StartX=6.75 StartY=105 StartZ=0 EndX=6.75 EndY=76.5 EndZ=0
    g5: LineSegment StartX=88.25 StartY=105 StartZ=0 EndX=88.25 EndY=76.5 EndZ=0
    g6: GeomPoint X=47.5 Y=105 Z=0
    g7: Circle CenterX=-118 CenterY=93 CenterZ=0 NormalX=0 NormalY=0 NormalZ=1 AngleXU=0 Radius=6
    g8: Circle CenterX=118 CenterY=93 CenterZ=0 NormalX=0 NormalY=0 NormalZ=1 AngleXU=0 Radius=6
    g9: ArcOfCircle CenterX=-86.75 CenterY=76.5 CenterZ=0 NormalX=0 NormalY=0 NormalZ=1 AngleXU=0 Radius=1.5 StartAngle=3.14159 EndAngle=4.71239
    g10: ArcOfCircle CenterX=-8.25 CenterY=76.5 CenterZ=0 NormalX=0 NormalY=0 NormalZ=1 AngleXU=0 Radius=1.5 StartAngle=4.71239 EndAngle=6.28319
    g11: LineSegment StartX=-86.75 StartY=75 StartZ=0 EndX=-8.25 EndY=75 EndZ=0
    g12: LineSegment StartX=-88.25 StartY=105 StartZ=0 EndX=-6.75 EndY=105 EndZ=0
    g13: LineSegment StartX=-6.75 StartY=105 StartZ=0 EndX=-6.75 EndY=76.5 EndZ=0
    g14: LineSegment StartX=-88.25 StartY=105 StartZ=0 EndX=-88.25 EndY=76.5 EndZ=0
    g15: GeomPoint X=-47.5 Y=105 Z=0
    g16: ArcOfCircle CenterX=86.75 CenterY=-76.5 CenterZ=0 NormalX=0 NormalY=0 NormalZ=1 AngleXU=0 Radius=1.5 StartAngle=0 EndAngle=1.5708
    g17: ArcOfCircle CenterX=8.25 CenterY=-76.5 CenterZ=0 NormalX=0 NormalY=0 NormalZ=1 AngleXU=0 Radius=1.5 StartAngle=1.5708 EndAngle=3.14159
    g18: LineSegment StartX=86.75 StartY=-75 StartZ=0 EndX=8.25 EndY=-75 EndZ=0
    g19: LineSegment StartX=88.25 StartY=-105 StartZ=0 EndX=6.75 EndY=-105 EndZ=0
    g20: LineSegment StartX=6.75 StartY=-105 StartZ=0 EndX=6.75 EndY=-76.5 EndZ=0
    g21: LineSegment StartX=88.25 StartY=-105 StartZ=0 EndX=88.25 EndY=-76.5 EndZ=0
    g22: GeomPoint X=47.5 Y=-105 Z=0
    g23: Circle CenterX=-118 CenterY=-93 CenterZ=0 NormalX=0 NormalY=0 NormalZ=1 AngleXU=0 Radius=6
    g24: Circle CenterX=118 CenterY=-93 CenterZ=0 NormalX=0 NormalY=0 NormalZ=1 AngleXU=0 Radius=6
    g25: ArcOfCircle CenterX=-86.75 CenterY=-76.5 CenterZ=0 NormalX=0 NormalY=0 NormalZ=1 AngleXU=0 Radius=1.5 StartAngle=1.5708 EndAngle=3.14159
    g26: ArcOfCircle CenterX=-8.25 CenterY=-76.5 CenterZ=0 NormalX=0 NormalY=0 NormalZ=1 AngleXU=0 Radius=1.5 StartAngle=0 EndAngle=1.5708
    g27: LineSegment StartX=-86.75 StartY=-75 StartZ=0 EndX=-8.25 EndY=-75 EndZ=0
    g28: LineSegment StartX=-88.25 StartY=-105 StartZ=0 EndX=-6.75 EndY=-105 EndZ=0
    g29: LineSegment StartX=-6.75 StartY=-105 StartZ=0 EndX=-6.75 EndY=-76.5 EndZ=0
    g30: LineSegment StartX=-88.25 StartY=-105 StartZ=0 EndX=-88.25 EndY=-76.5 EndZ=0
    g31: GeomPoint X=-47.5 Y=-105 Z=0
  constraints (65):
    c: Tangent(g0,g2) = 1.5708
    c: Tangent(g2,g1) = 1.5708
    c: Equal(g0,g1)
    c: Horizontal(g2)
    c: Horizontal(g3)
    c: Vertical(g5)
    c: Vertical(g4)
    c: Tangent(g0,g5) = 1.5708
    c: Tangent(g1,g4) = -1.5708
    c: Coincident(g5,g3)
    c: Coincident(g3,g4)
    c: Symmetric(g3,g3,g6)
    c: Radius(g1) = 1.5
    c: Distance(g1,g3) = 30
    c: Diameter(g7) = 12
    c: DistanceY(g-1,g7) = 93
    c: DistanceX(g7,g-1) = 118
    c: DistanceY(g-1,g3) = 105
    c: DistanceX(g3,g3) = 81.5
    c: DistanceX(g-1,g3) = 6.75
    c: Diameter(g8) = 12
    c: Tangent(g9,g11) = -1.5708
    c: Tangent(g11,g10) = -1.5708
    c: Equal(g9,g10)
    c: Horizontal(g11)
    c: Horizontal(g12)
    c: Vertical(g14)
    c: Vertical(g13)
    c: Tangent(g9,g14) = -1.5708
    c: Tangent(g10,g13) = 1.5708
    c: Coincident(g14,g12)
    c: Coincident(g12,g13)
    c: Symmetric(g12,g12,g15)
    c: Radius(g10) = 1.5
    c: Distance(g10,g12) = 30
    c: Tangent(g16,g18) = -1.5708
    c: Tangent(g18,g17) = -1.5708
    c: Equal(g16,g17)
    c: Horizontal(g18)
    c: Horizontal(g19)
    c: Vertical(g21)
    c: Vertical(g20)
    c: Tangent(g16,g21) = -1.5708
    c: Tangent(g17,g20) = 1.5708
    c: Coincident(g21,g19)
    c: Coincident(g19,g20)
    c: Symmetric(g19,g19,g22)
    c: Radius(g17) = 1.5
    c: Distance(g17,g19) = 30
    c: Diameter(g23) = 12
    c: Diameter(g24) = 12
    c: Tangent(g25,g27) = 1.5708
    c: Tangent(g27,g26) = 1.5708
    c: Equal(g25,g26)
    c: Horizontal(g27)
    c: Horizontal(g28)
    c: Vertical(g30)
    c: Vertical(g29)
    c: Tangent(g25,g30) = 1.5708
    c: Tangent(g26,g29) = -1.5708
    c: Coincident(g30,g28)
    c: Coincident(g28,g29)
    c: Symmetric(g28,g28,g31)
    c: Radius(g26) = 1.5
    c: Distance(g26,g28) = 30
FEATURE [PartDesign::Pocket] Pocket021
  BaseFeature = -> Pad018
  Direction = (0,0,-1)
  Length = 20
  Length2 = 20
  Profile = -> Sketch_004
  ReferenceAxis = -> Sketch_004 [N_Axis]
  Type = 4
FEATURE [PartDesign::Pocket] Pocket022
  BaseFeature = -> Pocket021
  Direction = (0,0,-1)
  Length = 20
  Length2 = 20
  Profile = -> Sketch035
  ReferenceAxis = -> Sketch035 [N_Axis]
  Type = 4
FEATURE [PartDesign::Body] Body064  label="перегородка_ползуна"
  Group = -> [Sketch035,Pad018,Block_ribb002,Sketch_004,Pocket021,Pocket022]
  Origin = -> Origin065
  Tip = -> Pocket022
COMPONENT P15 — recipe-attached ("Ползун_орто", modeled in this document).
Construction recipe (the document's own serialized feature program — sketch geometry with constraints, then the solid features built on it; lengths are millimeters unless a unit is written):

FEATURE [Sketcher::SketchObject] Sketch037
  FullyConstrained = true
  MapMode = 5
  Support = -> [XY_Plane061]
  sketch-geometry (10):
    g0: Circle CenterX=0 CenterY=0 CenterZ=0 NormalX=0 NormalY=0 NormalZ=1 AngleXU=0 Radius=57
    g1: Circle CenterX=0 CenterY=0 CenterZ=0 NormalX=0 NormalY=0 NormalZ=1 AngleXU=0 Radius=62
    g2: LineSegment StartX=62 StartY=55 StartZ=0 EndX=62 EndY=-75 EndZ=0
    g3: LineSegment StartX=62 StartY=-75 StartZ=0 EndX=-62 EndY=-75 EndZ=0
    g4: LineSegment StartX=-62 StartY=-75 StartZ=0 EndX=-62 EndY=55 EndZ=0
    g5: ArcOfCircle CenterX=0 CenterY=-70.5229 CenterZ=0 NormalX=0 NormalY=0 NormalZ=1 AngleXU=0 Radius=140 StartAngle=1.11201 EndAngle=2.02958
    g6: GeomPoint X=-62 Y=0 Z=0
    g7: ArcOfCircle CenterX=0 CenterY=-182.163 CenterZ=0 NormalX=0 NormalY=0 NormalZ=1 AngleXU=0 Radius=120 StartAngle=1.10403 EndAngle=2.03756
    g8: LineSegment StartX=62 StartY=-75 StartZ=0 EndX=54 EndY=-75 EndZ=0
    g9: LineSegment StartX=-54 StartY=-75 StartZ=0 EndX=-62 EndY=-75 EndZ=0
  constraints (27):
    c: Diameter(g0) = 114
    c: Coincident(g1,g0)
    c: Coincident(g0,g-1)
    c: Diameter(g1) = 124
    c: Coincident(g2,g3)
    c: Coincident(g3,g4)
    c: Vertical(g2)
    c: Vertical(g4)
    c: Symmetric(g3,g2,g-2)
    c: PointOnObject(g5,g-2)
    c: Coincident(g5,g4)
    c: Coincident(g5,g2)
    c: PointOnObject(g6,g-1)
    c: PointOnObject(g6,g1)
    c: PointOnObject(g6,g4)
    c: DistanceY(g2,g2) = 130
    c: Radius(g5) = 140
    c: DistanceY(g2,g0) = 75
    c: PointOnObject(g7,g-2)
    c: PointOnObject(g7,g3)
    c: PointOnObject(g7,g3)
    c: Coincident(g9,g4)
    c: Coincident(g9,g7)
    c: Coincident(g8,g7)
    c: Coincident(g8,g2)
    c: Radius(g7) = 120
    c: DistanceX(g9,g9) = 8
FEATURE [PartDesign::Pad] Pad019
  Direction = (0,0,1)
  Length = 11
  Length2 = 10
  Midplane = true
  Profile = -> Sketch037
  ReferenceAxis = -> Sketch037 [N_Axis]
  Type = 0
FEATURE [PartDesign::CoordinateSystem] Shtok002
  AttacherType = Attacher::AttachEngine3D
  MapMode = 11
  Placement = pos=(0,0,0) rot=(0,0,1;1.5708rad)
  Support = -> [Sketch037]
FEATURE [PartDesign::Body] Body065  label="Ползун_орто"
  Group = -> [Sketch037,Pad019,Shtok002]
  Origin = -> Origin066
  Tip = -> Pad019
COMPONENT P16 — recipe-attached ("направляющая_орто_ползуна", modeled in this document).
Construction recipe (the document's own serialized feature program — sketch geometry with constraints, then the solid features built on it; lengths are millimeters unless a unit is written):

FEATURE [Sketcher::SketchObject] Sketch038
  FullyConstrained = true
  MapMode = 5
  Support = -> [XY_Plane061]
  sketch-geometry (26):
    g0: LineSegment StartX=-103 StartY=-65 StartZ=0 EndX=103 EndY=-65 EndZ=0
    g1: LineSegment StartX=103 StartY=-65 StartZ=0 EndX=103 EndY=65 EndZ=0
    g2: LineSegment StartX=103 StartY=65 StartZ=0 EndX=-103 EndY=65 EndZ=0
    g3: LineSegment StartX=-103 StartY=65 StartZ=0 EndX=-103 EndY=-65 EndZ=0
    g4: ArcOfCircle CenterX=0 CenterY=40 CenterZ=0 NormalX=0 NormalY=0 NormalZ=1 AngleXU=0 Radius=20.25 StartAngle=1.05267 EndAngle=2.08892
    g5: ArcOfCircle CenterX=0 CenterY=0 CenterZ=0 NormalX=0 NormalY=0 NormalZ=1 AngleXU=0 Radius=55 StartAngle=2.08892 EndAngle=4.19427
    g6: ArcOfCircle CenterX=0 CenterY=0 CenterZ=0 NormalX=0 NormalY=0 NormalZ=1 AngleXU=0 Radius=55 StartAngle=5.23051 EndAngle=7.33586
    g7: ArcOfCircle CenterX=0 CenterY=-40 CenterZ=0 NormalX=0 NormalY=0 NormalZ=1 AngleXU=0 Radius=20.25 StartAngle=4.19427 EndAngle=5.23051
    g8: LineSegment StartX=-27.2388 StartY=47.7813 StartZ=0 EndX=-10.0288 EndY=57.5922 EndZ=0
    g9: LineSegment StartX=10.0288 StartY=57.5922 StartZ=0 EndX=27.2388 EndY=47.7813 EndZ=0
    g10: LineSegment StartX=-27.2388 StartY=-47.7812 StartZ=0 EndX=-10.0288 EndY=-57.5922 EndZ=0
    g11: LineSegment StartX=10.0288 StartY=-57.5922 StartZ=0 EndX=27.2388 EndY=-47.7812 EndZ=0
    g12: LineSegment StartX=-99 StartY=69.5 StartZ=0 EndX=99 EndY=69.5 EndZ=0
    g13: LineSegment StartX=-103 StartY=65 StartZ=0 EndX=-103 EndY=65.5 EndZ=0
    g14: LineSegment StartX=103 StartY=65.5 StartZ=0 EndX=103 EndY=65 EndZ=0
    g15: ArcOfCircle CenterX=-99 CenterY=65.5 CenterZ=0 NormalX=0 NormalY=0 NormalZ=1 AngleXU=0 Radius=4 StartAngle=1.5708 EndAngle=3.14159
    g16: ArcOfCircle CenterX=99 CenterY=65.5 CenterZ=0 NormalX=0 NormalY=0 NormalZ=1 AngleXU=0 Radius=4 StartAngle=4e-16 EndAngle=1.5708
    g17: ArcOfCircle CenterX=-99 CenterY=-65.5 CenterZ=0 NormalX=0 NormalY=0 NormalZ=1 AngleXU=0 Radius=4 StartAngle=3.14159 EndAngle=4.71239
    g18: LineSegment StartX=-103 StartY=-65 StartZ=0 EndX=-103 EndY=-65.5 EndZ=0
    g19: LineSegment StartX=-99 StartY=-69.5 StartZ=0 EndX=99 EndY=-69.5 EndZ=0
    g20: ArcOfCircle CenterX=99 CenterY=-65.5 CenterZ=0 NormalX=0 NormalY=0 NormalZ=1 AngleXU=0 Radius=4 StartAngle=4.71239 EndAngle=6.28319
    g21: LineSegment StartX=103 StartY=-65.5 StartZ=0 EndX=103 EndY=-65 EndZ=0
    g22: Circle CenterX=-95 CenterY=55 CenterZ=0 NormalX=0 NormalY=0 NormalZ=1 AngleXU=0 Radius=3
    g23: Circle CenterX=95 CenterY=55 CenterZ=0 NormalX=0 NormalY=0 NormalZ=1 AngleXU=0 Radius=3
    g24: Circle CenterX=-95 CenterY=-55 CenterZ=0 NormalX=0 NormalY=0 NormalZ=1 AngleXU=0 Radius=3
    g25: Circle CenterX=95 CenterY=-55 CenterZ=0 NormalX=0 NormalY=0 NormalZ=1 AngleXU=0 Radius=3
  constraints (58):
    c: Coincident(g0,g1)
    c: Coincident(g1,g2)
    c: Coincident(g2,g3)
    c: Coincident(g3,g0)
    c: Horizontal(g0)
    c: Vertical(g1)
    c: Symmetric(g2,g1,g-2)
    c: Symmetric(g2,g0,g-1)
    c: DistanceX(g2,g2) = 206
    c: PointOnObject(g4,g-2)
    c: Diameter(g4) = 40.5
    c: Equal(g4,g7)
    c: Symmetric(g4,g7,g-1)
    c: Equal(g5,g6)
    c: Tangent(g5,g10) = -1.5708
    c: Tangent(g5,g8) = 1.5708
    c: Tangent(g4,g8) = 1.5708
    c: Tangent(g4,g9) = 1.5708
    c: Tangent(g7,g11) = -1.5708
    c: Tangent(g7,g10) = -1.5708
    c: Tangent(g6,g9) = 1.5708
    c: Tangent(g6,g11) = -1.5708
    c: Distance(g-1,g4) = 40
    c: DistanceY(g1,g1) = 130
    c: Radius(g6) = 55
    c: Coincident(g5,g-1)
    c: Coincident(g6,g5)
    c: Coincident(g13,g3)
    c: Coincident(g14,g1)
    c: Tangent(g13,g15) = 1.5708
    c: Tangent(g12,g15) = 1.5708
    c: Tangent(g12,g16) = 1.5708
    c: Tangent(g14,g16) = 1.5708
    c: Vertical(g13)
    c: Vertical(g14)
    c: Symmetric(g15,g16,g-2)
    c: DistanceY(g1,g12) = 4.5
    c: Radius(g16) = 4
    c: Tangent(g18,g17) = -1.5708
    c: Tangent(g19,g17) = -1.5708
    c: Tangent(g19,g20) = -1.5708
    c: Vertical(g18)
    c: Symmetric(g17,g20,g-2)
    c: Symmetric(g17,g15,g-1)
    c: Coincident(g18,g3)
    c: Coincident(g21,g1)
    c: Vertical(g21)
    c: Equal(g21,g18)
    c: Coincident(g20,g21)
    c: Equal(g22,g23)
    c: Equal(g23,g25)
    c: Equal(g25,g24)
    c: Diameter(g23) = 6
    c: Symmetric(g22,g23,g-2)
    c: Symmetric(g24,g25,g-2)
    c: Symmetric(g24,g22,g-1)
    c: DistanceY(g24,g22) = 110
    c: DistanceX(g24,g25) = 190
FEATURE [PartDesign::Pad] Pad020
  Direction = (0,0,1)
  Length = 22.5
  Length2 = 5.5
  Midplane = true
  Profile = -> Sketch038
  ReferenceAxis = -> Sketch038 [N_Axis]
  Type = 4
FEATURE [PartDesign::CoordinateSystem] Shtok003
  AttacherType = Attacher::AttachEngine3D
  MapMode = 2
  Support = -> [Sketch038]
FEATURE [Sketcher::SketchObject] Sketch061
  FullyConstrained = false
  MapMode = 5
  Placement = pos=(0,0,22.5) rot=(0,0,1;0rad)
  Support = -> [Pad020]
  sketch-geometry (5):
    g0: Circle CenterX=0 CenterY=0 CenterZ=0 NormalX=0 NormalY=0 NormalZ=1 AngleXU=0 Radius=8.25
    g1: LineSegment StartX=-79.3827 StartY=20 StartZ=0 EndX=79.3827 EndY=20 EndZ=0
    g2: LineSegment StartX=79.3827 StartY=20 StartZ=0 EndX=79.3827 EndY=-20 EndZ=0
    g3: LineSegment StartX=79.3827 StartY=-20 StartZ=0 EndX=-79.3827 EndY=-20 EndZ=0
    g4: LineSegment StartX=-79.3827 StartY=-20 StartZ=0 EndX=-79.3827 EndY=20 EndZ=0
  constraints (12):
    c: Coincident(g0,g-1)
    c: Diameter(g0) = 16.5
    c: Coincident(g1,g2)
    c: Coincident(g2,g3)
    c: Coincident(g3,g4)
    c: Coincident(g4,g1)
    c: Horizontal(g1)
    c: Horizontal(g3)
    c: Vertical(g2)
    c: Vertical(g4)
    c: Symmetric(g3,g1,g0)
    c: DistanceY(g2,g2) = 40
FEATURE [PartDesign::Pad] Pad032
  BaseFeature = -> Pad020
  Direction = (0,0,1)
  Length = 16
  Length2 = 10
  Profile = -> Sketch061
  ReferenceAxis = -> Sketch061 [N_Axis]
  Reversed = true
  Type = 0
FEATURE [PartDesign::Body] Body066  label="направляющая_орто_ползуна"
  Group = -> [Sketch038,Pad020,Shtok003,Sketch061,Pad032]
  Origin = -> Origin067
  Tip = -> Pad032
COMPONENT P17 — recipe-attached ("Поршень003", modeled in this document).
Construction recipe (the document's own serialized feature program — sketch geometry with constraints, then the solid features built on it; lengths are millimeters unless a unit is written):

FEATURE [Sketcher::SketchObject] Sketch041
  FullyConstrained = true
  MapMode = 5
  Support = -> [XY_Plane069]
  sketch-geometry (6):
    g0: Circle CenterX=0 CenterY=85 CenterZ=0 NormalX=0 NormalY=0 NormalZ=1 AngleXU=0 Radius=11.5
    g1: LineSegment StartX=-45.5 StartY=147 StartZ=0 EndX=45.5 EndY=147 EndZ=0
    g2: LineSegment StartX=-45.5 StartY=147 StartZ=0 EndX=-45.5 EndY=51 EndZ=0
    g3: LineSegment StartX=0 StartY=51 StartZ=0 EndX=-45.5 EndY=51 EndZ=0
    g4: LineSegment StartX=45.5 StartY=147 StartZ=0 EndX=45.5 EndY=51 EndZ=0
    g5: LineSegment StartX=0 StartY=51 StartZ=0 EndX=45.5 EndY=51 EndZ=0
  constraints (15):
    c: Coincident(g2,g1)
    c: Vertical(g2)
    c: Symmetric(g1,g1,g-2)
    c: DistanceX(g1,g1) = 91
    c: PointOnObject(g3,g-2)
    c: Vertical(g4)
    c: Block(g0)
    c: Coincident(g1,g4)
    c: DistanceY(g0,g1) = 62
    c: DistanceY(g3,g0) = 34
    c: Horizontal(g3)
    c: Coincident(g2,g3)
    c: Coincident(g5,g3)
    c: Coincident(g5,g4)
    c: Horizontal(g5)
FEATURE [PartDesign::Pad] Pad021
  Direction = (0,0,1)
  Length = 100
  Length2 = 10
  Midplane = true
  Profile = -> Sketch041
  ReferenceAxis = -> Sketch041 [N_Axis]
  Type = 0
FEATURE [PartDesign::Body] Body070  label="Поршень003"
  Group = -> [Sketch041,Pad021]
  Origin = -> Origin071
  Tip = -> Pad021
COMPONENT P18 — recipe-attached ("Поршень_2T_92mm", modeled in this document).
Construction recipe (the document's own serialized feature program — sketch geometry with constraints, then the solid features built on it; lengths are millimeters unless a unit is written):

FEATURE [PartDesign::CoordinateSystem] Piston001
  AttacherType = Attacher::AttachEngine3D
  MapMode = 2
  Placement = pos=(0,0,0) rot=(1,0,0;1.5708rad)
  Support = -> [XZ_Plane071]
FEATURE [Sketcher::SketchObject] Sketch042
  FullyConstrained = false
  MapMode = 5
  Placement = pos=(0,0,0) rot=(1,0,0;1.5708rad)
  Support = -> [XZ_Plane071]
  sketch-geometry (2):
    g0: GeomPoint X=-87.5 Y=-1.47e-14 Z=0
    g1: Circle CenterX=0 CenterY=0 CenterZ=0 NormalX=0 NormalY=0 NormalZ=1 AngleXU=0 Radius=45.5
  constraints (2):
    c: Coincident(g1,g-1)
    c: Diameter(g1) = 91
FEATURE [PartDesign::Pad] Pad022
  Direction = (0,-1,-2e-16)
  Length = 200
  Length2 = 10
  Placement = pos=(0,0,0) rot=(1,0,0;1.5708rad)
  Profile = -> Sketch042
  ReferenceAxis = -> Sketch042 [N_Axis]
  Reversed = true
  Type = 0
FEATURE [PartDesign::Boolean] Boolean004
  BaseFeature = -> Pad022
  Group = -> [Body070]
  Type = 2
FEATURE [Sketcher::SketchObject] Sketch043
  FullyConstrained = true
  MapMode = 5
  Placement = pos=(0,0,0) rot=(1,0,0;1.5708rad)
  sketch-geometry (2):
    g0: Circle CenterX=0 CenterY=0 CenterZ=0 NormalX=0 NormalY=0 NormalZ=1 AngleXU=0 Radius=41
    g1: Circle CenterX=0 CenterY=0 CenterZ=0 NormalX=0 NormalY=0 NormalZ=1 AngleXU=0 Radius=15
  constraints (4):
    c: Coincident(g0,g-1)
    c: Diameter(g0) = 82
    c: Coincident(g1,g0)
    c: Diameter(g1) = 30
FEATURE [PartDesign::Pocket] Pocket025
  BaseFeature = -> Boolean004
  Direction = (0,1,-2e-16)
  Length = 138
  Length2 = 5
  Profile = -> Sketch043
  ReferenceAxis = -> Sketch043 [N_Axis]
  Type = 0
FEATURE [Sketcher::SketchObject] Sketch044
  FullyConstrained = false
  MapMode = 5
  Placement = pos=(0,0,0) rot=(1,0,0;1.5708rad)
  Support = -> [XZ_Plane071]
  sketch-geometry (3):
    g0: GeomPoint X=-87.5 Y=-1.47e-14 Z=0
    g1: Circle CenterX=0 CenterY=0 CenterZ=0 NormalX=0 NormalY=0 NormalZ=1 AngleXU=0 Radius=43
    g2: Circle CenterX=0 CenterY=0 CenterZ=0 NormalX=0 NormalY=0 NormalZ=1 AngleXU=0 Radius=47.5
  constraints (4):
    c: Coincident(g1,g-1)
    c: Coincident(g2,g1)
    c: Diameter(g1) = 86
    c: Diameter(g2) = 95
FEATURE [PartDesign::Pocket] Pocket026  label="Pocket002-ring002"
  BaseFeature = -> Pocket025
  Direction = (0,1,2e-16)
  Length = 143
  Length2 = -141
  Profile = -> Sketch044
  ReferenceAxis = -> Sketch044 [N_Axis]
  Type = 4
FEATURE [PartDesign::Pocket] Pocket027  label="Pocket003-ring003"
  BaseFeature = -> Pocket026
  Direction = (0,1,2e-16)
  Length = 138
  Length2 = -136
  Profile = -> Sketch044
  ReferenceAxis = -> Sketch044 [N_Axis]
  Type = 4
FEATURE [PartDesign::Pocket] Pocket028  label="Pocket004-komp-ring001"
  BaseFeature = -> Pocket027
  Direction = (0,1,2e-16)
  Length = 55
  Length2 = -58
  Profile = -> Sketch044
  ReferenceAxis = -> Sketch044 [N_Axis]
  Type = 4
FEATURE [Sketcher::SketchObject] Sketch049
  FullyConstrained = true
  MapMode = 5
  Placement = pos=(0,0,0) rot=(1,0,0;1.5708rad)
  sketch-geometry (1):
    g0: Circle CenterX=0 CenterY=0 CenterZ=0 NormalX=0 NormalY=0 NormalZ=1 AngleXU=0 Radius=30
  constraints (2):
    c: Coincident(g0,g-1)
    c: Diameter(g0) = 60
FEATURE [PartDesign::Pocket] Pocket030  label="Pocket023-conrod-polzun001"
  BaseFeature = -> Pocket028
  Direction = (0,1,-2e-16)
  Length = 110
  Length2 = 5
  Profile = -> Sketch049
  ReferenceAxis = -> Sketch049 [N_Axis]
  Type = 0
FEATURE [PartDesign::Pocket] Pocket031  label="Pocket002-ring3"
  BaseFeature = -> Pocket030
  Direction = (0,1,2e-16)
  Length = 63
  Length2 = -61
  Profile = -> Sketch044
  ReferenceAxis = -> Sketch044 [N_Axis]
  Type = 4
FEATURE [Sketcher::SketchObject] Sketch052
  FullyConstrained = true
  MapMode = 5
  Placement = pos=(0,0,0) rot=(1,0,0;1.5708rad)
  sketch-geometry (1):
    g0: Circle CenterX=0 CenterY=0 CenterZ=0 NormalX=0 NormalY=0 NormalZ=1 AngleXU=0 Radius=11
  constraints (2):
    c: Coincident(g0,g-1)
    c: Diameter(g0) = 22
FEATURE [PartDesign::Pocket] Pocket032
  BaseFeature = -> Pocket031
  Direction = (0,1,-2e-16)
  Length = 130
  Length2 = 5
  Profile = -> Sketch052
  ReferenceAxis = -> Sketch052 [N_Axis]
  Type = 4
FEATURE [PartDesign::Body] Body071  label="Поршень_2T_92mm"
  Group = -> [Sketch042,Pad022,Boolean004,Sketch043,Pocket025,Sketch044,Pocket026,Pocket027,Pocket028,Piston001,Sketch049,Pocket030,Pocket031,Sketch052,Pocket032]
  Origin = -> Origin072
  Tip = -> Pocket032
COMPONENT P19 — recipe-attached ("Цилиндр", modeled in this document).
Construction recipe (the document's own serialized feature program — sketch geometry with constraints, then the solid features built on it; lengths are millimeters unless a unit is written):

FEATURE [PartDesign::CoordinateSystem] Cylynder001
  AttacherType = Attacher::AttachEngine3D
  MapMode = 2
  Placement = pos=(0,0,25) rot=(0,0,1;0rad)
  Support = -> [Body073]
FEATURE [Sketcher::SketchObject] Sketch046
  FullyConstrained = false
  MapMode = 5
  Placement = pos=(0,0,0) rot=(1,0,0;1.5708rad)
  Support = -> [XZ_Plane072]
  sketch-geometry (12):
    g0: ArcOfCircle CenterX=-53 CenterY=1.3e-15 CenterZ=0 NormalX=0 NormalY=0 NormalZ=1 AngleXU=0 Radius=46 StartAngle=1.5708 EndAngle=4.71239
    g1: ArcOfCircle CenterX=0 CenterY=0 CenterZ=0 NormalX=0 NormalY=0 NormalZ=1 AngleXU=0 Radius=46 StartAngle=4.71239 EndAngle=7.85398
    g2: LineSegment StartX=-53 StartY=-46 StartZ=0 EndX=-7.1e-15 EndY=-46 EndZ=0
    g3: LineSegment StartX=0 StartY=46 StartZ=0 EndX=-53 EndY=46 EndZ=0
    g4: LineSegment StartX=-222.305 StartY=100 StartZ=0 EndX=222.305 EndY=100 EndZ=0
    g5: LineSegment StartX=222.305 StartY=100 StartZ=0 EndX=222.305 EndY=-100 EndZ=0
    g6: LineSegment StartX=222.305 StartY=-100 StartZ=0 EndX=-222.305 EndY=-100 EndZ=0
    g7: LineSegment StartX=-222.305 StartY=-100 StartZ=0 EndX=-222.305 EndY=100 EndZ=0
    g8: Circle CenterX=-53 CenterY=1.3e-15 CenterZ=0 NormalX=0 NormalY=0 NormalZ=1 AngleXU=0 Radius=46
    g9: Circle CenterX=0 CenterY=0 CenterZ=0 NormalX=0 NormalY=0 NormalZ=1 AngleXU=0 Radius=46
    g10: Circle CenterX=53 CenterY=0 CenterZ=0 NormalX=0 NormalY=0 NormalZ=1 AngleXU=0 Radius=46
    g11: LineSegment StartX=0 StartY=46 StartZ=0 EndX=53 EndY=46 EndZ=0
  constraints (28):
    c: Tangent(g0,g2) = -1.5708
    c: Tangent(g2,g1) = -1.5708
    c: Tangent(g1,g3) = -1.5708
    c: Tangent(g3,g0) = -1.5708
    c: Equal(g0,g1)
    c: Horizontal(g2)
    c: DistanceY(g0,g0) = 92
    c: Coincident(g4,g5)
    c: Coincident(g5,g6)
    c: Coincident(g6,g7)
    c: Coincident(g7,g4)
    c: Horizontal(g6)
    c: Vertical(g7)
    c: DistanceY(g5,g5) = 200
    c: Symmetric(g5,g4,g-1)
    c: Symmetric(g4,g4,g-2)
    c: Coincident(g8,g0)
    c: Coincident(g9,g1)
    c: Equal(g8,g0)
    c: Equal(g9,g1)
    c: Coincident(g9,g-1)
    c: PointOnObject(g10,g-1)
    c: Equal(g9,g10)
    c: Coincident(g11,g1)
    c: PointOnObject(g11,g10)
    c: Horizontal(g11)
    c: Equal(g3,g11)
    c: DistanceX(g8,g10) = 106
FEATURE [PartDesign::Pad] Pad023
  Direction = (0,-1,-2e-16)
  Length = 300
  Length2 = 10
  Placement = pos=(0,0,0) rot=(1,0,0;1.5708rad)
  Profile = -> Sketch046
  ReferenceAxis = -> Sketch046 [N_Axis]
  Type = 0
FEATURE [PartDesign::Boolean] Boolean005
  BaseFeature = -> Pad023
  Group = -> [Body073]
  Type = 2
FEATURE [Sketcher::SketchObject] Sketch047
  FullyConstrained = true
  MapMode = 5
  Support = -> [XY_Plane071]
  sketch-geometry (2):
    g0: Circle CenterX=-137 CenterY=-90 CenterZ=0 NormalX=0 NormalY=0 NormalZ=1 AngleXU=0 Radius=30.5
    g1: Circle CenterX=137 CenterY=-90 CenterZ=0 NormalX=0 NormalY=0 NormalZ=1 AngleXU=0 Radius=30.5
  constraints (5):
    c: Diameter(g0) = 61
    c: Symmetric(g0,g1,g-2)
    c: DistanceY(g0,g-1) = 90
    c: DistanceX(g0,g1) = 274
    c: Equal(g1,g0)
FEATURE [Sketcher::SketchObject] Sketch048
  FullyConstrained = false
  MapMode = 5
  Support = -> [XY_Plane071]
  sketch-geometry (17):
    g0: LineSegment StartX=72.5228 StartY=-25.9373 StartZ=0 EndX=72.5228 EndY=-109 EndZ=0
    g1: LineSegment StartX=72.5228 StartY=-109 StartZ=0 EndX=-72.5228 EndY=-109 EndZ=0
    g2: LineSegment StartX=-72.5228 StartY=-109 StartZ=0 EndX=-72.5228 EndY=-25.9373 EndZ=0
    g3: LineSegment StartX=-72.5228 StartY=-25.9373 StartZ=0 EndX=-160.839 EndY=-25.9373 EndZ=0
    g4: LineSegment StartX=-160.839 StartY=-25.9373 StartZ=0 EndX=-160.839 EndY=-150.037 EndZ=0
    g5: LineSegment StartX=-160.839 StartY=-150.037 StartZ=0 EndX=-95 EndY=-174 EndZ=0
    g6: LineSegment StartX=-95 StartY=-174 StartZ=0 EndX=-95 EndY=-193.155 EndZ=0
    g7: LineSegment StartX=-95 StartY=-193.155 StartZ=0 EndX=-179.18 EndY=-162.516 EndZ=0
    g8: LineSegment StartX=-179.18 StartY=-162.516 StartZ=0 EndX=-179.18 EndY=-8.0171 EndZ=0
    g9: LineSegment StartX=-179.18 StartY=-8.0171 StartZ=0 EndX=179.18 EndY=-8.0171 EndZ=0
    g10: LineSegment StartX=179.18 StartY=-8.0171 StartZ=0 EndX=179.18 EndY=-156.131 EndZ=0
    g11: LineSegment StartX=179.18 StartY=-156.131 StartZ=0 EndX=95 EndY=-186.77 EndZ=0
    g12: LineSegment StartX=95 StartY=-186.77 StartZ=0 EndX=95 EndY=-174 EndZ=0
    g13: LineSegment StartX=95 StartY=-174 StartZ=0 EndX=160.839 EndY=-150.037 EndZ=0
    g14: LineSegment StartX=160.839 StartY=-150.037 StartZ=0 EndX=160.839 EndY=-25.9373 EndZ=0
    g15: LineSegment StartX=160.839 StartY=-25.9373 StartZ=0 EndX=72.5228 EndY=-25.9373 EndZ=0
    g16: LineSegment StartX=-72.5228 StartY=-25.9373 StartZ=0 EndX=72.5228 EndY=-25.9373 EndZ=0
  constraints (43):
    c: Coincident(g0,g1)
    c: Coincident(g1,g2)
    c: Vertical(g0)
    c: Vertical(g2)
    c: DistanceY(g0,g-1) = 109
    c: Symmetric(g1,g0,g-2)
    c: Coincident(g2,g3)
    c: Horizontal(g3)
    c: Coincident(g3,g4)
    c: Vertical(g4)
    c: Coincident(g4,g5)
    c: Coincident(g5,g6)
    c: Vertical(g6)
    c: Coincident(g6,g7)
    c: Coincident(g7,g8)
    c: Vertical(g8)
    c: Coincident(g8,g9)
    c: Coincident(g9,g10)
    c: Vertical(g10)
    c: Coincident(g10,g11)
    c: Coincident(g11,g12)
    c: Vertical(g12)
    c: Coincident(g12,g13)
    c: Coincident(g13,g14)
    c: Vertical(g14)
    c: Coincident(g14,g15)
    c: Coincident(g15,g0)
    c: Horizontal(g15)
    c: Symmetric(g8,g9,g-2)
    c: Equal(g3,g15)
    c: Parallel(g5,g7)
    c: Parallel(g13,g11)
    c: Distance(g12,g11) = 12
    c: Angle(g5) = -0.349066
    c: Angle(g13) = 0.349066
    c: Symmetric(g5,g12,g-2)
    c: DistanceX(g5,g12) = 190
    c: DistanceY(g5,g-1) = 174
    c: Block(g9)
    c: Distance(g5,g7) = 18
    c: Coincident(g16,g3)
    c: Coincident(g16,g15)
    c: Horizontal(g16)
FEATURE [PartDesign::Pocket] Pocket029
  BaseFeature = -> Boolean005
  Direction = (0,0,-1)
  Length = 60
  Length2 = 5
  Midplane = true
  Profile = -> Sketch048
  ReferenceAxis = -> Sketch048 [N_Axis]
  Type = 0
FEATURE [Sketcher::SketchObject] Sketch050
  FullyConstrained = false
  MapMode = 5
  Placement = pos=(0,0,0) rot=(0.57735,0.57735,0.57735;2.0944rad)
  Support = -> [YZ_Plane072]
  sketch-geometry (4):
    g0: LineSegment StartX=-184.527 StartY=91.8627 StartZ=0 EndX=-217.963 EndY=0 EndZ=0
    g1: LineSegment StartX=-217.963 StartY=0 StartZ=0 EndX=-202 EndY=0 EndZ=0
    g2: LineSegment StartX=-202 StartY=0 StartZ=0 EndX=-168.565 EndY=91.8627 EndZ=0
    g3: LineSegment StartX=-168.565 StartY=91.8627 StartZ=0 EndX=-184.527 EndY=91.8627 EndZ=0
  constraints (11):
    c: Coincident(g0,g1)
    c: Horizontal(g1)
    c: Coincident(g1,g2)
    c: Coincident(g2,g3)
    c: Coincident(g3,g0)
    c: Horizontal(g3)
    c: Equal(g1,g3)
    c: Angle(g2) = 1.22173
    c: Distance(g1,g0) = 15
    c: PointOnObject(g1,g-1)
    c: DistanceX(g1,g-1) = 202
FEATURE [PartDesign::Body] Body072  label="Цилиндр"
  Group = -> [Sketch046,Pad023,Boolean005,Cylynder001,Sketch047,Sketch048,Pocket029,Sketch050]
  Origin = -> Origin073
  Placement = pos=(0,0,25) rot=(0,0,1;0rad)
  Tip = -> Pocket029
COMPONENT P20 — recipe-attached ("Body073", modeled in this document).
Construction recipe (the document's own serialized feature program — sketch geometry with constraints, then the solid features built on it; lengths are millimeters unless a unit is written):

FEATURE [Sketcher::SketchObject] Sketch045
  FullyConstrained = true
  MapMode = 5
  Support = -> [XY_Plane072]
  sketch-geometry (11):
    g0: LineSegment StartX=-120 StartY=252 StartZ=0 EndX=120 EndY=252 EndZ=0
    g1: LineSegment StartX=120 StartY=252 StartZ=0 EndX=120 EndY=-252 EndZ=0
    g2: LineSegment StartX=120 StartY=-252 StartZ=0 EndX=-120 EndY=-252 EndZ=0
    g3: LineSegment StartX=-120 StartY=-252 StartZ=0 EndX=-120 EndY=252 EndZ=0
    g4: LineSegment StartX=-120 StartY=252 StartZ=0 EndX=-120 EndY=75.5 EndZ=0
    g5: LineSegment StartX=-120 StartY=75.5 StartZ=0 EndX=120 EndY=75.5 EndZ=0
    g6: LineSegment StartX=120 StartY=75.5 StartZ=0 EndX=120 EndY=252 EndZ=0
    g7: LineSegment StartX=-120 StartY=-252 StartZ=0 EndX=-120 EndY=-75.5 EndZ=0
    g8: LineSegment StartX=-120 StartY=-75.5 StartZ=0 EndX=120 EndY=-75.5 EndZ=0
    g9: LineSegment StartX=120 StartY=-75.5 StartZ=0 EndX=120 EndY=-252 EndZ=0
    g10: LineSegment StartX=120 StartY=-75.5 StartZ=0 EndX=120 EndY=-252 EndZ=0
  constraints (28):
    c: Coincident(g0,g1)
    c: Coincident(g1,g2)
    c: Coincident(g2,g3)
    c: Coincident(g3,g0)
    c: Horizontal(g2)
    c: Vertical(g1)
    c: Symmetric(g0,g0,g-2)
    c: Symmetric(g0,g2,g-1)
    c: Coincident(g0,g4)
    c: PointOnObject(g4,g3)
    c: Coincident(g4,g5)
    c: PointOnObject(g5,g1)
    c: Horizontal(g5)
    c: Coincident(g5,g6)
    c: Coincident(g6,g0)
    c: Coincident(g2,g7)
    c: PointOnObject(g7,g3)
    c: Coincident(g7,g8)
    c: PointOnObject(g8,g1)
    c: Horizontal(g8)
    c: Coincident(g8,g9)
    c: Coincident(g9,g2)
    c: Equal(g9,g6)
    c: DistanceX(g2,g2) = 240
    c: Coincident(g10,g8)
    c: Coincident(g10,g2)
    c: DistanceY(g2,g-1) = 252
    c: DistanceY(g7,g7) = 176.5
FEATURE [PartDesign::Pad] Pad024
  Direction = (0,0,1)
  Length = 28
  Length2 = 78
  Midplane = true
  Profile = -> Sketch045
  ReferenceAxis = -> Sketch045 [N_Axis]
  Type = 4
FEATURE [PartDesign::Body] Body073
  Group = -> [Sketch045,Pad024]
  Origin = -> Origin074
  Placement = pos=(0,0,25) rot=(0,0,1;0rad)
  Tip = -> Pad024
COMPONENT P21 — recipe-attached ("Cam_001", modeled in this document).
Construction recipe (the document's own serialized feature program — sketch geometry with constraints, then the solid features built on it; lengths are millimeters unless a unit is written):

FEATURE [Sketcher::SketchObject] Sketch056
  FullyConstrained = false
  MapMode = 5
  Support = -> [XY_Plane074]
  expr: Constraints[0] = <<assm4_Main_BSM_M3_r80>>#<<Dim_table>>.crank_dia2 + 0.5
  expr: Constraints[13] = <<assm4_Main_BSM_M3_r80>>#<<Dim_table>>.crank_len
  expr: Constraints[4] = <<assm4_Main_BSM_M3_r80>>#<<Dim_table>>.crank_len
  expr: Constraints[5] = <<assm4_Main_BSM_M3_r80>>#<<Dim_table>>.ecc_dia
  sketch-geometry (7):
    g0: Circle CenterX=0 CenterY=20 CenterZ=0 NormalX=0 NormalY=0 NormalZ=1 AngleXU=0 Radius=29.25
    g1: LineSegment StartX=0 StartY=20 StartZ=0 EndX=1.8e-15 EndY=40 EndZ=0
    g2: Circle CenterX=1.8e-15 CenterY=40 CenterZ=0 NormalX=0 NormalY=0 NormalZ=1 AngleXU=0 Radius=52
    g3: ArcOfCircle CenterX=-3.4e-15 CenterY=40.1625 CenterZ=0 NormalX=0 NormalY=0 NormalZ=1 AngleXU=0 Radius=37.8247 StartAngle=0.61368 EndAngle=2.52791
    g4: ArcOfCircle CenterX=0 CenterY=4.30054 CenterZ=0 NormalX=0 NormalY=0 NormalZ=1 AngleXU=0 Radius=55.9864 StartAngle=1.11517 EndAngle=2.02642
    g5: ArcOfCircle CenterX=-26.8353 CenterY=59.0656 CenterZ=0 NormalX=0 NormalY=0 NormalZ=1 AngleXU=0 Radius=5 StartAngle=2.52791 EndAngle=5.16801
    g6: ArcOfCircle CenterX=26.8353 CenterY=59.0656 CenterZ=0 NormalX=0 NormalY=0 NormalZ=1 AngleXU=0 Radius=5 StartAngle=4.25677 EndAngle=6.89687
  constraints (15):
    c: Diameter(g0) = 58.5
    c: Coincident(g1,g0)
    c: Angle(g1) = 1.5708
    c: Coincident(g2,g1)
    c: DistanceY(g0,g2) = 20
    c: Diameter(g2) = 104
    c: PointOnObject(g4,g-2)
    c: Tangent(g3,g5) = -1.5708
    c: Tangent(g4,g5) = 1.5708
    c: Tangent(g3,g6) = -1.5708
    c: Tangent(g4,g6) = 1.5708
    c: Symmetric(g5,g6,g-2)
    c: PointOnObject(g0,g-2)
    c: DistanceY(g-1,g0) = 20
    c: Radius(g5) = 5
FEATURE [PartDesign::Pad] Pad027
  Direction = (0,0,1)
  Length = 10
  Length2 = 10
  Profile = -> Sketch056
  ReferenceAxis = -> Sketch056 [N_Axis]
  Type = 0
FEATURE [PartDesign::Body] Body075  label="Cam_001"
  Group = -> [Sketch056,Pad027]
  Origin = -> Origin076
  Placement = pos=(0,-20,13) rot=(0,0,1;0rad)
  Tip = -> Pad027
COMPONENT P22 — recipe-attached ("корпус_нижний", modeled in this document).
Construction recipe (the document's own serialized feature program — sketch geometry with constraints, then the solid features built on it; lengths are millimeters unless a unit is written):

FEATURE [Sketcher::SketchObject] Sketch060
  FullyConstrained = true
  Placement = pos=(0,0,0) rot=(1,0,0;3.14159rad)
  expr: Constraints[11] = <<Dim_table>>.crank_dia1 + <<Dim_table>>.zazor
  expr: Constraints[14] = <<Dim_table>>.crank_dia2
  expr: Constraints[15] = <<Dim_table>>.inter_shaft_len / 2
  expr: Constraints[6] = <<Dim_table>>.inter_shaft_len
  expr: Constraints[7] = <<Dim_table>>.crank_dia1 * 1.5
  sketch-geometry (7):
    g0: ArcOfCircle CenterX=0 CenterY=0 CenterZ=0 NormalX=0 NormalY=0 NormalZ=1 AngleXU=0 Radius=18.75 StartAngle=1.5708 EndAngle=4.71239
    g1: ArcOfCircle CenterX=46 CenterY=-1.3e-15 CenterZ=0 NormalX=0 NormalY=0 NormalZ=1 AngleXU=0 Radius=18.75 StartAngle=4.71239 EndAngle=7.85398
    g2: LineSegment StartX=-2.01e-14 StartY=-18.75 StartZ=0 EndX=46 EndY=-18.75 EndZ=0
    g3: LineSegment StartX=46 StartY=18.75 StartZ=0 EndX=-8.67644e-11 EndY=18.75 EndZ=0
    g4: Circle CenterX=0 CenterY=0 CenterZ=0 NormalX=0 NormalY=0 NormalZ=1 AngleXU=0 Radius=12.75
    g5: Circle CenterX=46 CenterY=-1.3e-15 CenterZ=0 NormalX=0 NormalY=0 NormalZ=1 AngleXU=0 Radius=12.75
    g6: Circle CenterX=23 CenterY=0 CenterZ=0 NormalX=0 NormalY=0 NormalZ=1 AngleXU=0 Radius=6.25
  constraints (16):
    c: Tangent(g0,g2) = -1.5708
    c: Tangent(g2,g1) = -1.5708
    c: Tangent(g1,g3) = -1.5708
    c: Tangent(g3,g0) = -1.5708
    c: Equal(g0,g1)
    c: Horizontal(g2)
    c: DistanceX(g0,g1) = 46
    c: Diameter(g0) = 37.5
    c: Coincident(g4,g0)
    c: Coincident(g5,g1)
    c: Equal(g4,g5)
    c: Diameter(g4) = 25.5
    c: Coincident(g0,g-1)
    c: PointOnObject(g6,g-1)
    c: Diameter(g6) = 12.5
    c: DistanceX(g0,g6) = 23
FEATURE [Sketcher::SketchObject] Sketch064
  FullyConstrained = true
  Placement = pos=(0,0,0) rot=(1,0,0;3.14159rad)
  expr: Constraints[1] = <<Dim_table>>.inter_shaft_len
  expr: Constraints[2] = <<Dim_table>>.inter_shaft_len * 1.2
  expr: Constraints[9] = <<Dim_table>>.fillet_r
  sketch-geometry (4):
    g0: ArcOfCircle CenterX=0 CenterY=0 CenterZ=0 NormalX=0 NormalY=0 NormalZ=1 AngleXU=0 Radius=27.6 StartAngle=0.680867 EndAngle=5.60232
    g1: ArcOfCircle CenterX=46 CenterY=0 CenterZ=0 NormalX=0 NormalY=0 NormalZ=1 AngleXU=0 Radius=27.6 StartAngle=3.82246 EndAngle=8.74391
    g2: ArcOfCircle CenterX=23 CenterY=18.6322 CenterZ=0 NormalX=0 NormalY=0 NormalZ=1 AngleXU=0 Radius=2 StartAngle=3.82246 EndAngle=5.60232
    g3: ArcOfCircle CenterX=23 CenterY=-18.6322 CenterZ=0 NormalX=0 NormalY=0 NormalZ=1 AngleXU=0 Radius=2 StartAngle=0.680867 EndAngle=2.46073
  constraints (11):
    c: PointOnObject(g1,g-1)
    c: Distance(g0,g1) = 46
    c: Diameter(g0) = 55.2
    c: Equal(g0,g1)
    c: Tangent(g0,g2) = 1.5708
    c: Tangent(g1,g2) = 1.5708
    c: Tangent(g0,g3) = 1.5708
    c: Tangent(g1,g3) = 1.5708
    c: Equal(g3,g2)
    c: Radius(g2) = 2
    c: Coincident(g0,g-1)
FEATURE [Sketcher::SketchObject] Sketch074
  FullyConstrained = true
  MapMode = 5
  Support = -> [XY_Plane076]
  expr: Constraints[14] = <<Dim_table>>.inter_shaft_len * 2.15
  expr: Constraints[15] = <<Dim_table>>.ecc_dia * 1.2
  expr: Constraints[16] = <<Dim_table>>.inter_shaft_len * 1.85
  expr: Constraints[22] = <<Dim_table>>.inter_shaft_len / 2
  expr: Constraints[37] = <<Dim_table>>.inter_shaft_len * 2.35
  expr: Constraints[38] = <<Dim_table>>.crank_dia2
  expr: Constraints[39] = <<Dim_table>>.inter_shaft_len * 2
  expr: Constraints[45] = <<Dim_table>>.inter_shaft_len / 2
  expr: Constraints[53] = <<Dim_table>>.axle_hole_dia
  expr: Constraints[56] = <<Dim_table>>.inter_shaft_len
  expr: Constraints[58] = <<Dim_table>>.crank_dia1 + <<Dim_table>>.zazor
  expr: Constraints[60] = <<Dim_table>>.crank_dia2
  sketch-geometry (27):
    g0: LineSegment StartX=-4.85 StartY=-42.55 StartZ=0 EndX=50.85 EndY=-42.55 EndZ=0
    g1: LineSegment StartX=72.45 StartY=-20.95 StartZ=0 EndX=72.45 EndY=20.95 EndZ=0
    g2: LineSegment StartX=50.85 StartY=42.55 StartZ=0 EndX=-4.85 EndY=42.55 EndZ=0
    g3: LineSegment StartX=-26.45 StartY=20.95 StartZ=0 EndX=-26.45 EndY=-20.95 EndZ=0
    g4: ArcOfCircle CenterX=-4.85 CenterY=20.95 CenterZ=0 NormalX=0 NormalY=0 NormalZ=1 AngleXU=0 Radius=21.6 StartAngle=1.5708 EndAngle=3.14159
    g5: ArcOfCircle CenterX=50.85 CenterY=20.95 CenterZ=0 NormalX=0 NormalY=0 NormalZ=1 AngleXU=0 Radius=21.6 StartAngle=0 EndAngle=1.5708
    g6: ArcOfCircle CenterX=-4.85 CenterY=-20.95 CenterZ=0 NormalX=0 NormalY=0 NormalZ=1 AngleXU=0 Radius=21.6 StartAngle=3.14159 EndAngle=4.71239
    g7: ArcOfCircle CenterX=50.85 CenterY=-20.95 CenterZ=0 NormalX=0 NormalY=0 NormalZ=1 AngleXU=0 Radius=21.6 StartAngle=4.71239 EndAngle=6.28319
    g8: LineSegment StartX=-26.45 StartY=-20.95 StartZ=0 EndX=72.45 EndY=20.95 EndZ=0
    g9: GeomPoint X=23 Y=0 Z=0
    g10: ArcOfCircle CenterX=-24.8 CenterY=39.75 CenterZ=0 NormalX=0 NormalY=0 NormalZ=1 AngleXU=0 Radius=6.25 StartAngle=1.5708 EndAngle=3.14159
    g11: LineSegment StartX=70.8 StartY=46 StartZ=0 EndX=-24.8 EndY=46 EndZ=0
    g12: ArcOfCircle CenterX=70.8 CenterY=39.75 CenterZ=0 NormalX=0 NormalY=0 NormalZ=1 AngleXU=0 Radius=6.25 StartAngle=0 EndAngle=1.5708
    g13: LineSegment StartX=77.05 StartY=-39.75 StartZ=0 EndX=77.05 EndY=39.75 EndZ=0
    g14: ArcOfCircle CenterX=70.8 CenterY=-39.75 CenterZ=0 NormalX=0 NormalY=0 NormalZ=1 AngleXU=0 Radius=6.25 StartAngle=4.71239 EndAngle=6.28319
    g15: LineSegment StartX=-24.8 StartY=-46 StartZ=0 EndX=70.8 EndY=-46 EndZ=0
    g16: ArcOfCircle CenterX=-24.8 CenterY=-39.75 CenterZ=0 NormalX=0 NormalY=0 NormalZ=1 AngleXU=0 Radius=6.25 StartAngle=3.14159 EndAngle=4.71239
    g17: LineSegment StartX=-31.05 StartY=39.75 StartZ=0 EndX=-31.05 EndY=-39.75 EndZ=0
    g18: LineSegment StartX=-24.8 StartY=46 StartZ=0 EndX=70.8 EndY=-46 EndZ=0
    g19: GeomPoint X=23 Y=0 Z=0
    g20: Circle CenterX=-24.8 CenterY=39.75 CenterZ=0 NormalX=0 NormalY=0 NormalZ=1 AngleXU=0 Radius=1.5
    g21: Circle CenterX=70.8 CenterY=39.75 CenterZ=0 NormalX=0 NormalY=0 NormalZ=1 AngleXU=0 Radius=1.5
    g22: Circle CenterX=-24.8 CenterY=-39.75 CenterZ=0 NormalX=0 NormalY=0 NormalZ=1 AngleXU=0 Radius=1.5
    g23: Circle CenterX=70.8 CenterY=-39.75 CenterZ=0 NormalX=0 NormalY=0 NormalZ=1 AngleXU=0 Radius=1.5
    g24: Circle CenterX=0 CenterY=0 CenterZ=0 NormalX=0 NormalY=0 NormalZ=1 AngleXU=0 Radius=12.75
    g25: Circle CenterX=46 CenterY=0 CenterZ=0 NormalX=0 NormalY=0 NormalZ=1 AngleXU=0 Radius=12.75
    g26: Circle CenterX=23 CenterY=0 CenterZ=0 NormalX=0 NormalY=0 NormalZ=1 AngleXU=0 Radius=6.25
  constraints (61):
    c: Horizontal(g0)
    c: Horizontal(g2)
    c: Vertical(g1)
    c: Vertical(g3)
    c: Tangent(g2,g4) = -1.5708
    c: Tangent(g3,g4) = -1.5708
    c: Tangent(g2,g5) = -1.5708
    c: Tangent(g1,g5) = -1.5708
    c: Tangent(g3,g6) = -1.5708
    c: Tangent(g0,g6) = -1.5708
    c: Tangent(g0,g7) = -1.5708
    c: Tangent(g1,g7) = -1.5708
    c: Equal(g4,g5)
    c: Equal(g5,g7)
    c: DistanceX(g3,g1) = 98.9
    c: Diameter(g4) = 43.2
    c: DistanceY(g0,g2) = 85.1
    c: Symmetric(g2,g0,g-1)
    c: Coincident(g8,g3)
    c: Coincident(g8,g1)
    c: PointOnObject(g9,g-1)
    c: PointOnObject(g9,g8)
    c: DistanceX(g-1,g9) = 23
    c: Horizontal(g15)
    c: Horizontal(g11)
    c: Vertical(g13)
    c: Vertical(g17)
    c: Tangent(g11,g10) = -1.5708
    c: Tangent(g17,g10) = -1.5708
    c: Tangent(g11,g12) = -1.5708
    c: Tangent(g13,g12) = -1.5708
    c: Tangent(g17,g16) = -1.5708
    c: Tangent(g15,g16) = -1.5708
    c: Tangent(g15,g14) = -1.5708
    c: Tangent(g13,g14) = -1.5708
    c: Equal(g10,g12)
    c: Equal(g12,g14)
    c: DistanceX(g17,g13) = 108.1
    c: Diameter(g10) = 12.5
    c: DistanceY(g15,g11) = 92
    c: Symmetric(g10,g16,g-1)
    c: Coincident(g18,g10)
    c: Coincident(g18,g14)
    c: PointOnObject(g19,g-1)
    c: PointOnObject(g19,g18)
    c: DistanceX(g-1,g19) = 23
    c: Coincident(g20,g10)
    c: Coincident(g21,g12)
    c: Coincident(g22,g16)
    c: Coincident(g23,g14)
    c: Equal(g22,g23)
    c: Equal(g23,g21)
    c: Equal(g21,g20)
    c: Diameter(g20) = 3
    c: Coincident(g24,g-1)
    c: PointOnObject(g25,g-1)
    c: DistanceX(g24,g25) = 46
    c: Equal(g25,g24)
    c: Diameter(g24) = 25.5
    c: Coincident(g26,g9)
    c: Diameter(g26) = 12.5
FEATURE [PartDesign::CoordinateSystem] Shtok004
  AttacherType = Attacher::AttachEngine3D
  MapMode = 2
  Support = -> [Sketch074]
FEATURE [PartDesign::Pad] Pad042
  Direction = (0,0,1)
  Length = 15
  Length2 = 10
  Profile = -> Sketch074
  ReferenceAxis = -> Sketch074 [N_Axis]
  Reversed = true
  Type = 0
FEATURE [PartDesign::Pad] Pad043
  BaseFeature = -> Pad042
  Direction = (0,0,-1)
  Length = 25
  Length2 = 10
  Profile = -> Sketch060
  ReferenceAxis = -> Sketch060 [N_Axis]
  Type = 0
FEATURE [PartDesign::Pocket] Pocket036
  BaseFeature = -> Pad043
  Direction = (0,0,1)
  Length = 10.5
  Length2 = 5
  Profile = -> Sketch064
  ReferenceAxis = -> Sketch064 [N_Axis]
  Reversed = true
  Type = 0
FEATURE [PartDesign::Body] Body076  label="корпус_нижний"
  Group = -> [Shtok004,Sketch060,Sketch064,Sketch074,Pad042,Pad043,Pocket036]
  Origin = -> Origin077
  Tip = -> Pocket036
COMPONENT P23 — recipe-attached ("проставка_корпуса", modeled in this document).
Construction recipe (the document's own serialized feature program — sketch geometry with constraints, then the solid features built on it; lengths are millimeters unless a unit is written):

FEATURE [Sketcher::SketchObject] Sketch058
  FullyConstrained = false
  MapMode = 5
  Support = -> [XY_Plane077]
  sketch-geometry (32):
    g0: LineSegment StartX=-103 StartY=-65 StartZ=0 EndX=103 EndY=-65 EndZ=0
    g1: LineSegment StartX=103 StartY=-65 StartZ=0 EndX=103 EndY=65 EndZ=0
    g2: LineSegment StartX=103 StartY=65 StartZ=0 EndX=-103 EndY=65 EndZ=0
    g3: LineSegment StartX=-103 StartY=65 StartZ=0 EndX=-103 EndY=-65 EndZ=0
    g4: LineSegment StartX=-99 StartY=69.5 StartZ=0 EndX=99 EndY=69.5 EndZ=0
    g5: LineSegment StartX=-103 StartY=65 StartZ=0 EndX=-103 EndY=65.5 EndZ=0
    g6: LineSegment StartX=103 StartY=65.5 StartZ=0 EndX=103 EndY=65 EndZ=0
    g7: ArcOfCircle CenterX=-99 CenterY=65.5 CenterZ=0 NormalX=0 NormalY=0 NormalZ=1 AngleXU=0 Radius=4 StartAngle=1.5708 EndAngle=3.14159
    g8: ArcOfCircle CenterX=99 CenterY=65.5 CenterZ=0 NormalX=0 NormalY=0 NormalZ=1 AngleXU=0 Radius=4 StartAngle=-9e-16 EndAngle=1.5708
    g9: ArcOfCircle CenterX=-99 CenterY=-65.5 CenterZ=0 NormalX=0 NormalY=0 NormalZ=1 AngleXU=0 Radius=4 StartAngle=3.14159 EndAngle=4.71239
    g10: LineSegment StartX=-103 StartY=-65 StartZ=0 EndX=-103 EndY=-65.5 EndZ=0
    g11: LineSegment StartX=-99 StartY=-69.5 StartZ=0 EndX=99 EndY=-69.5 EndZ=0
    g12: ArcOfCircle CenterX=99 CenterY=-65.5 CenterZ=0 NormalX=0 NormalY=0 NormalZ=1 AngleXU=0 Radius=4 StartAngle=4.71239 EndAngle=6.28319
    g13: LineSegment StartX=103 StartY=-65.5 StartZ=0 EndX=103 EndY=-65 EndZ=0
    g14: Circle CenterX=-95 CenterY=55 CenterZ=0 NormalX=0 NormalY=0 NormalZ=1 AngleXU=0 Radius=3
    g15: Circle CenterX=95 CenterY=55 CenterZ=0 NormalX=0 NormalY=0 NormalZ=1 AngleXU=0 Radius=3
    g16: Circle CenterX=-95 CenterY=-55 CenterZ=0 NormalX=0 NormalY=0 NormalZ=1 AngleXU=0 Radius=3
    g17: Circle CenterX=95 CenterY=-55 CenterZ=0 NormalX=0 NormalY=0 NormalZ=1 AngleXU=0 Radius=3
    g18: Circle CenterX=0 CenterY=0 CenterZ=0 NormalX=0 NormalY=0 NormalZ=1 AngleXU=0 Radius=32.25
    g19: LineSegment StartX=-103 StartY=-65 StartZ=0 EndX=-91.9993 EndY=-65 EndZ=0
    g20: LineSegment StartX=-91.9993 StartY=-65 StartZ=0 EndX=-91.9993 EndY=-49.9993 EndZ=0
    g21: LineSegment StartX=-91.9993 StartY=-49.9993 StartZ=0 EndX=-103 EndY=-49.9993 EndZ=0
    g22: LineSegment StartX=-103 StartY=-49.9993 StartZ=0 EndX=-103 EndY=-65 EndZ=0
    g23: LineSegment StartX=103 StartY=-65 StartZ=0 EndX=91.9993 EndY=-65 EndZ=0
    g24: LineSegment StartX=91.9993 StartY=-65 StartZ=0 EndX=91.9993 EndY=-49.9993 EndZ=0
    g25: LineSegment StartX=91.9993 StartY=-49.9993 StartZ=0 EndX=103 EndY=-49.9993 EndZ=0
    g26: LineSegment StartX=103 StartY=-49.9993 StartZ=0 EndX=103 EndY=-65 EndZ=0
    g27: LineSegment StartX=103 StartY=65 StartZ=0 EndX=91.9993 EndY=65 EndZ=0
    g28: LineSegment StartX=91.9993 StartY=65 StartZ=0 EndX=91.9993 EndY=49.9993 EndZ=0
    g29: LineSegment StartX=91.9993 StartY=49.9993 StartZ=0 EndX=103 EndY=49.9993 EndZ=0
    g30: LineSegment StartX=103 StartY=49.9993 StartZ=0 EndX=103 EndY=65 EndZ=0
    g31: Circle CenterX=-95 CenterY=55 CenterZ=0 NormalX=0 NormalY=0 NormalZ=1 AngleXU=0 Radius=8
  constraints (75):
    c: Coincident(g0,g1)
    c: Coincident(g1,g2)
    c: Coincident(g2,g3)
    c: Coincident(g3,g0)
    c: Horizontal(g0)
    c: Vertical(g1)
    c: Symmetric(g2,g1,g-2)
    c: Symmetric(g2,g0,g-1)
    c: DistanceX(g2,g2) = 206
    c: DistanceY(g1,g1) = 130
    c: Coincident(g5,g3)
    c: Coincident(g6,g1)
    c: Tangent(g5,g7) = 1.5708
    c: Tangent(g4,g7) = 1.5708
    c: Tangent(g4,g8) = 1.5708
    c: Tangent(g6,g8) = 1.5708
    c: Vertical(g5)
    c: Vertical(g6)
    c: Symmetric(g7,g8,g-2)
    c: DistanceY(g1,g4) = 4.5
    c: Radius(g8) = 4
    c: Tangent(g10,g9) = -1.5708
    c: Tangent(g11,g9) = -1.5708
    c: Tangent(g11,g12) = -1.5708
    c: Vertical(g10)
    c: Symmetric(g9,g12,g-2)
    c: Symmetric(g9,g7,g-1)
    c: Coincident(g10,g3)
    c: Coincident(g13,g1)
    c: Vertical(g13)
    c: Equal(g13,g10)
    c: Coincident(g12,g13)
    c: Equal(g14,g15)
    c: Equal(g15,g17)
    c: Equal(g17,g16)
    c: Diameter(g15) = 6
    c: Symmetric(g14,g15,g-2)
    c: Symmetric(g16,g17,g-2)
    c: Symmetric(g16,g14,g-1)
    c: DistanceY(g16,g14) = 110
    c: DistanceX(g16,g17) = 190
    c: Coincident(g18,g-1)
    c: Diameter(g18) = 64.5
    c: Coincident(g19,g20)
    c: Coincident(g20,g21)
    c: Coincident(g21,g22)
    c: Coincident(g22,g19)
    c: Horizontal(g19)
    c: Horizontal(g21)
    c: Vertical(g20)
    c: Vertical(g22)
    c: Coincident(g19,g0)
    c: Coincident(g23,g24)
    c: Coincident(g24,g25)
    c: Coincident(g25,g26)
    c: Coincident(g26,g23)
    c: Horizontal(g23)
    c: Horizontal(g25)
    c: Vertical(g24)
    c: Vertical(g26)
    c: Coincident(g23,g0)
    c: Coincident(g27,g28)
    c: Coincident(g28,g29)
    c: Coincident(g29,g30)
    c: Coincident(g30,g27)
    c: Horizontal(g27)
    c: Horizontal(g29)
    c: Vertical(g28)
    c: Vertical(g30)
    c: Coincident(g27,g1)
    c: Equal(g25,g29)
    c: Equal(g28,g24)
    c: Equal(g24,g20)
    c: Coincident(g31,g14)
    c: Tangent(g31,g3)
FEATURE [PartDesign::Pad] Pad029
  Direction = (0,0,1)
  Length = 25
  Length2 = 28.5
  Midplane = true
  Profile = -> Sketch058
  ReferenceAxis = -> Sketch058 [N_Axis]
  Type = 4
FEATURE [PartDesign::CoordinateSystem] Shtok005
  AttacherType = Attacher::AttachEngine3D
  MapMode = 2
  Support = -> [Sketch058]
FEATURE [PartDesign::Body] Body077  label="проставка_корпуса"
  Group = -> [Sketch058,Pad029,Shtok005]
  Origin = -> Origin078
  Tip = -> Pad029
COMPONENT P24 — recipe-attached ("Cam_002", modeled in this document).
Construction recipe (the document's own serialized feature program — sketch geometry with constraints, then the solid features built on it; lengths are millimeters unless a unit is written):

FEATURE [Sketcher::SketchObject] Sketch063
  FullyConstrained = true
  MapMode = 5
  Support = -> [XY_Plane079]
  expr: Constraints[0] = <<Dim_table>>.crank_dia2 + 0.5
  expr: Constraints[2] = <<Dim_table>>.crank_dia2 + 6
  expr: Constraints[4] = <<Dim_table>>.crank_len
  sketch-geometry (2):
    g0: Circle CenterX=0 CenterY=9.5 CenterZ=0 NormalX=0 NormalY=0 NormalZ=1 AngleXU=0 Radius=6.5
    g1: Circle CenterX=0 CenterY=9.5 CenterZ=0 NormalX=0 NormalY=0 NormalZ=1 AngleXU=0 Radius=9.25
  constraints (5):
    c: Diameter(g0) = 13
    c: Coincident(g1,g0)
    c: Diameter(g1) = 18.5
    c: PointOnObject(g0,g-2)
    c: Distance(g-1,g0) = 9.5
FEATURE [PartDesign::Pad] Pad033
  Direction = (0,0,1)
  Length = 10
  Length2 = 10
  Profile = -> Sketch063
  ReferenceAxis = -> Sketch063 [N_Axis]
  Type = 0
FEATURE [PartDesign::Body] Body078  label="Cam_002"
  Group = -> [Sketch063,Pad033]
  Origin = -> Origin079
  Placement = pos=(0,-20,-23) rot=(0,0,1;0rad)
  Tip = -> Pad033
COMPONENT P25 — recipe-attached ("Ползун_орто_новый_clone", modeled in this document).
Construction recipe (the document's own serialized feature program — sketch geometry with constraints, then the solid features built on it; lengths are millimeters unless a unit is written):

FEATURE [PartDesign::FeatureBase] Clone009
  BaseFeature = -> Body060
FEATURE [PartDesign::CoordinateSystem] Local_CS003
  AttacherType = Attacher::AttachEngine3D
  MapMode = 7
  Placement = pos=(57,-57,4.75) rot=(1,0,0;1.5708rad)
  Support = -> [Clone009]
FEATURE [PartDesign::Body] Body079  label="Ползун_орто_новый_clone"
  Group = -> [Clone009,Local_CS003]
  Origin = -> Origin080
  Tip = -> Clone009
COMPONENT P26 — recipe-attached ("Эксцентрик_clone", modeled in this document).
Construction recipe (the document's own serialized feature program — sketch geometry with constraints, then the solid features built on it; lengths are millimeters unless a unit is written):

FEATURE [PartDesign::FeatureBase] Clone010
  BaseFeature = -> Body001
FEATURE [PartDesign::CoordinateSystem] Local_CS
  AttacherType = Attacher::AttachEngine3D
FEATURE [PartDesign::Body] Body080  label="Эксцентрик_clone"
  Group = -> [Clone010,Local_CS]
  Origin = -> Origin081
  Tip = -> Clone010
COMPONENT P27 — recipe-attached ("направляющая_верхнего_ползуна(clone)", modeled in this document).
Construction recipe (the document's own serialized feature program — sketch geometry with constraints, then the solid features built on it; lengths are millimeters unless a unit is written):

FEATURE [PartDesign::FeatureBase] Clone011
  BaseFeature = -> ________________________
FEATURE [PartDesign::Boolean] Boolean006
  BaseFeature = -> Clone011
  Group = -> [Body082]
  Type = 0
FEATURE [PartDesign::CoordinateSystem] LCS_1
  AttacherType = Attacher::AttachEngine3D
  MapMode = 2
  Support = -> [Boolean006]
FEATURE [PartDesign::Body] Body081  label="направляющая_верхнего_ползуна(clone)"
  Group = -> [Clone011,Boolean006,LCS_1]
  Origin = -> Origin083
  Tip = -> Boolean006
COMPONENT P28 — recipe-attached ("Body082", modeled in this document).
Construction recipe (the document's own serialized feature program — sketch geometry with constraints, then the solid features built on it; lengths are millimeters unless a unit is written):

FEATURE [PartDesign::FeatureBase] Clone012
  BaseFeature = -> Extrude
FEATURE [PartDesign::Body] Body082
  Group = -> [Clone012]
  Origin = -> Origin085
  Tip = -> Clone012
COMPONENT P29 — recipe-attached ("crank_gear_01", modeled in this document).
Construction recipe (the document's own serialized feature program — sketch geometry with constraints, then the solid features built on it; lengths are millimeters unless a unit is written):

FEATURE [PartDesign::FeatureBase] BaseFeature
  BaseFeature = -> InvoluteGear006
FEATURE [PartDesign::CoordinateSystem] Local_CS005
  AttacherType = Attacher::AttachEngine3D
  AttachmentOffset = pos=(0,0,0) rot=(0,0,1;0.621337rad)
  MapMode = 2
  Placement = pos=(0,0,0) rot=(0,0,1;0.621337rad)
  Support = -> [BaseFeature]
FEATURE [PartDesign::Body] Body087  label="crank_gear_01"
  BaseFeature = -> InvoluteGear006
  Group = -> [BaseFeature,Local_CS005]
  Origin = -> Origin090
  Tip = -> BaseFeature
COMPONENT P30 — recipe-attached ("crank_int_gear_01", modeled in this document).
Construction recipe (the document's own serialized feature program — sketch geometry with constraints, then the solid features built on it; lengths are millimeters unless a unit is written):

FEATURE [PartDesign::FeatureBase] BaseFeature001
  BaseFeature = -> InternalInvoluteGear001
FEATURE [PartDesign::CoordinateSystem] Local_CS004
  AttacherType = Attacher::AttachEngine3D
  MapMode = 2
  Support = -> [BaseFeature001]
FEATURE [PartDesign::Body] Body088  label="crank_int_gear_01"
  BaseFeature = -> InternalInvoluteGear001
  Group = -> [BaseFeature001,Local_CS004]
  Origin = -> Origin091
  Tip = -> BaseFeature001
COMPONENT P31 — recipe-attached ("Inter_crank_gear01", modeled in this document).
Construction recipe (the document's own serialized feature program — sketch geometry with constraints, then the solid features built on it; lengths are millimeters unless a unit is written):

FEATURE [PartDesign::FeatureBase] BaseFeature002
  BaseFeature = -> InvoluteGear003
FEATURE [PartDesign::CoordinateSystem] Local_CS006
  AttacherType = Attacher::AttachEngine3D
  MapMode = 2
  Support = -> [BaseFeature002]
FEATURE [PartDesign::Body] Body089  label="Inter_crank_gear01"
  BaseFeature = -> InvoluteGear003
  Group = -> [BaseFeature002,Local_CS006]
  Origin = -> Origin092
  Tip = -> BaseFeature002
COMPONENT P32 — recipe-attached ("Шейка_и_щека_задняя", modeled in this document).
Construction recipe (the document's own serialized feature program — sketch geometry with constraints, then the solid features built on it; lengths are millimeters unless a unit is written):

FEATURE [Sketcher::SketchObject] Sketch071
  FullyConstrained = true
  MapMode = 5
  expr: Constraints[0] = <<Dim_table>>.crank_dia2
  expr: Constraints[3] = <<Dim_table>>.axle_hole_dia
  sketch-geometry (2):
    g0: Circle CenterX=0 CenterY=0 CenterZ=0 NormalX=0 NormalY=0 NormalZ=1 AngleXU=0 Radius=6.25
    g1: Circle CenterX=0 CenterY=0 CenterZ=0 NormalX=0 NormalY=0 NormalZ=1 AngleXU=0 Radius=1.5
  constraints (4):
    c: Diameter(g0) = 12.5
    c: Coincident(g0,g-1)
    c: Coincident(g1,g0)
    c: Diameter(g1) = 3
FEATURE [PartDesign::Pad] Pad039
  Direction = (0,0,1)
  Length = 10.25
  Length2 = 10
  Profile = -> Sketch071
  ReferenceAxis = -> Sketch071 [N_Axis]
  Type = 0
FEATURE [Sketcher::SketchObject] Sketch072
  FullyConstrained = true
  MapMode = 5
  Support = -> [XY_Plane094]
  expr: Constraints[17] = <<Dim_table>>.fillet_r
  expr: Constraints[18] = <<Dim_table>>.fillet_r
  expr: Constraints[21] = <<Dim_table>>.inter_shaft_len - <<Dim_table>>.zazor
  expr: Constraints[23] = <<Dim_table>>.axle_hole_dia
  expr: Constraints[24] = 70
  expr: Constraints[25] = <<Dim_table>>.crank_dia2 * 1.5
  expr: Constraints[26] = <<Dim_table>>.crank_len
  sketch-geometry (14):
    g0: ArcOfCircle CenterX=0 CenterY=0 CenterZ=0 NormalX=0 NormalY=0 NormalZ=1 AngleXU=0 Radius=22.75 StartAngle=0.0965354 EndAngle=3.04506
    g1: ArcOfCircle CenterX=-1e-15 CenterY=-9.5 CenterZ=0 NormalX=0 NormalY=0 NormalZ=1 AngleXU=0 Radius=9.375 StartAngle=3.49066 EndAngle=5.93412
    g2: LineSegment StartX=-8.80962 StartY=-12.7064 StartZ=0 EndX=8.80962 EndY=-12.7064 EndZ=0
    g3: LineSegment StartX=-20.6534 StartY=0 StartZ=0 EndX=-14.8348 EndY=0 EndZ=0
    g4: LineSegment StartX=-12.9554 StartY=-1.31596 StartZ=0 EndX=-8.80962 EndY=-12.7064 EndZ=0
    g5: LineSegment StartX=8.80962 StartY=-12.7064 StartZ=0 EndX=12.9554 EndY=-1.31596 EndZ=0
    g6: LineSegment StartX=14.8348 StartY=3.1e-15 StartZ=0 EndX=20.6534 EndY=3.1e-15 EndZ=0
    g7: ArcOfCircle CenterX=-14.8348 CenterY=-2 CenterZ=0 NormalX=0 NormalY=0 NormalZ=1 AngleXU=0 Radius=2 StartAngle=0.349066 EndAngle=1.5708
    g8: ArcOfCircle CenterX=14.8348 CenterY=-2 CenterZ=0 NormalX=0 NormalY=0 NormalZ=1 AngleXU=0 Radius=2 StartAngle=1.5708 EndAngle=2.79253
    g9: ArcOfCircle CenterX=20.6534 CenterY=2 CenterZ=0 NormalX=0 NormalY=0 NormalZ=1 AngleXU=0 Radius=2 StartAngle=4.71239 EndAngle=6.37972
    g10: ArcOfCircle CenterX=-20.6534 CenterY=2 CenterZ=0 NormalX=0 NormalY=0 NormalZ=1 AngleXU=0 Radius=2 StartAngle=3.04506 EndAngle=4.71239
    g11: Circle CenterX=0 CenterY=0 CenterZ=0 NormalX=0 NormalY=0 NormalZ=1 AngleXU=0 Radius=22.75
    g12: Circle CenterX=0 CenterY=0 CenterZ=0 NormalX=0 NormalY=0 NormalZ=1 AngleXU=0 Radius=1.5
    g13: Circle CenterX=-1e-15 CenterY=-9.5 CenterZ=0 NormalX=0 NormalY=0 NormalZ=1 AngleXU=0 Radius=1.5
  constraints (31):
    c: Coincident(g2,g1)
    c: Coincident(g2,g1)
    c: Horizontal(g2)
    c: Horizontal(g3)
    c: Horizontal(g6)
    c: Tangent(g4,g1) = -1.5708
    c: Tangent(g5,g1) = -1.5708
    c: Tangent(g3,g7) = 1.5708
    c: Tangent(g4,g7) = 1.5708
    c: Tangent(g6,g8) = 1.5708
    c: Tangent(g5,g8) = 1.5708
    c: Tangent(g6,g9) = -1.5708
    c: Tangent(g0,g9) = -1.5708
    c: Tangent(g0,g10) = -1.5708
    c: Tangent(g3,g10) = -1.5708
    c: Symmetric(g7,g8,g-2)
    c: Symmetric(g10,g9,g-2)
    c: Radius(g10) = 2
    c: Radius(g7) = 2
    c: Coincident(g0,g-1)
    c: Coincident(g11,g0)
    c: Diameter(g11) = 45.5
    c: Coincident(g12,g11)
    c: Diameter(g12) = 3
    c: Angle(g5) = 1.22173
    c: Diameter(g1) = 18.75
    c: DistanceY(g1,g12) = 9.5
    c: PointOnObject(g3,g-1)
    c: Coincident(g13,g1)
    c: Equal(g13,g12)
    c: Equal(g0,g11)
FEATURE [PartDesign::Pad] Pad040
  BaseFeature = -> Pad039
  Direction = (0,0,1)
  Length = 10
  Length2 = 10
  Profile = -> Sketch072
  ReferenceAxis = -> Sketch072 [N_Axis]
  Reversed = true
  Type = 0
FEATURE [PartDesign::Chamfer] Chamfer001
  Angle = 45
  Base = -> Pad040 [Edge14]
  BaseFeature = -> Pad040
  ChamferType = 0
  FlipDirection = false
  Size = 1.5
  Size2 = 1
  SupportTransform = false
  UseAllEdges = false
FEATURE [PartDesign::Body] Body090  label="Шейка_и_щека_задняя"
  Group = -> [Sketch071,Pad039,Sketch072,Pad040,Chamfer001]
  Origin = -> Origin093
  Placement = pos=(0,0,-6.5) rot=(0,0,1;0rad)
  Tip = -> Chamfer001
COMPONENT P33 — recipe-attached ("Шейка_и_щека_задняя_cl", modeled in this document).
Construction recipe (the document's own serialized feature program — sketch geometry with constraints, then the solid features built on it; lengths are millimeters unless a unit is written):

FEATURE [PartDesign::FeatureBase] Clone
  BaseFeature = -> Cut
FEATURE [PartDesign::CoordinateSystem] LCS_2
  AttacherType = Attacher::AttachEngine3D
  MapMode = 11
  Placement = pos=(0,0,-16.5) rot=(0,0,1;1.5708rad)
  Support = -> [Cut]
FEATURE [PartDesign::Body] Body091  label="Шейка_и_щека_задняя_cl"
  Group = -> [Clone,LCS_2]
  Origin = -> Origin094
  Tip = -> Clone
COMPONENT P34 — recipe-attached ("проставка_корпуса_штока1", modeled in this document).
Construction recipe (the document's own serialized feature program — sketch geometry with constraints, then the solid features built on it; lengths are millimeters unless a unit is written):

FEATURE [PartDesign::FeatureBase] BaseFeature003
  BaseFeature = -> Extrude001
FEATURE [PartDesign::CoordinateSystem] LCS_3
  AttacherType = Attacher::AttachEngine3D
  MapMode = 2
  Support = -> [BaseFeature003]
FEATURE [PartDesign::Body] Body092  label="проставка_корпуса_штока1"
  BaseFeature = -> Extrude001
  Group = -> [BaseFeature003,LCS_3]
  Origin = -> Origin096
  Tip = -> BaseFeature003
COMPONENT P35 — recipe-attached ("ручка", modeled in this document).
Construction recipe (the document's own serialized feature program — sketch geometry with constraints, then the solid features built on it; lengths are millimeters unless a unit is written):

FEATURE [Sketcher::SketchObject] Sketch078
  FullyConstrained = true
  MapMode = 5
  Support = -> [XY_Plane098]
  expr: Constraints[0] = <<Dim_table>>.crank_dia1
  expr: Constraints[20] = <<Dim_table>>.hex_size - <<Dim_table>>.zazor * 0.75
  sketch-geometry (8):
    g0: Circle CenterX=0 CenterY=0 CenterZ=0 NormalX=0 NormalY=0 NormalZ=1 AngleXU=0 Radius=12.5
    g1: LineSegment StartX=3.9332 StartY=6.8125 StartZ=0 EndX=-3.9332 EndY=6.8125 EndZ=0
    g2: LineSegment StartX=-3.9332 StartY=6.8125 StartZ=0 EndX=-7.8664 EndY=1.0836e-12 EndZ=0
    g3: LineSegment StartX=-7.8664 StartY=1.0839e-12 StartZ=0 EndX=-3.9332 EndY=-6.8125 EndZ=0
    g4: LineSegment StartX=-3.9332 StartY=-6.8125 StartZ=0 EndX=3.9332 EndY=-6.8125 EndZ=0
    g5: LineSegment StartX=3.9332 StartY=-6.8125 StartZ=0 EndX=7.8664 EndY=1.0836e-12 EndZ=0
    g6: LineSegment StartX=7.8664 StartY=1.0839e-12 StartZ=0 EndX=3.9332 EndY=6.8125 EndZ=0
    g7: Circle CenterX=0 CenterY=0 CenterZ=0 NormalX=0 NormalY=0 NormalZ=1 AngleXU=0 Radius=7.8664
  constraints (18):
    c: Diameter(g0) = 25
    c: Coincident(g1,g2)
    c: Coincident(g2,g3)
    c: Coincident(g3,g4)
    c: Coincident(g4,g5)
    c: Coincident(g5,g6)
    c: Coincident(g6,g1)
    c: Equal(g1, g2-g6) x5
    c: PointOnObject(g1,g7)
    c: PointOnObject(g2,g7)
    c: PointOnObject(g3,g7)
    c: PointOnObject(g4,g7)
    c: PointOnObject(g5,g7)
    c: PointOnObject(g6,g7)
    c: Coincident(g7,g0)
    c: Horizontal(g1)
    c: DistanceY(g3,g1) = 13.625
    c: Coincident(g0,g-1)
FEATURE [PartDesign::Pad] Pad046
  Direction = (0,0,1)
  Length = 22
  Length2 = 10
  Profile = -> Sketch078
  ReferenceAxis = -> Sketch078 [N_Axis]
  Type = 0
FEATURE [Sketcher::SketchObject] Sketch079
  FullyConstrained = true
  MapMode = 5
  Placement = pos=(0,0,22) rot=(0,0,1;0rad)
  Support = -> [Pad046]
  expr: Constraints[6] = <<Dim_table>>.crank_len * 3
  expr: Constraints[7] = <<Dim_table>>.crank_dia1 * 0.8
  expr: Constraints[8] = <<Dim_table>>.crank_dia1 * 0.4
  sketch-geometry (4):
    g0: ArcOfCircle CenterX=0 CenterY=0 CenterZ=0 NormalX=0 NormalY=0 NormalZ=1 AngleXU=0 Radius=10 StartAngle=1.39445 EndAngle=4.88874
    g1: ArcOfCircle CenterX=28.5 CenterY=0 CenterZ=0 NormalX=0 NormalY=0 NormalZ=1 AngleXU=0 Radius=5 StartAngle=4.88874 EndAngle=7.67763
    g2: LineSegment StartX=1.75439 StartY=-9.8449 StartZ=0 EndX=29.3772 EndY=-4.92245 EndZ=0
    g3: LineSegment StartX=29.3772 StartY=4.92245 StartZ=0 EndX=1.75439 EndY=9.8449 EndZ=0
  constraints (9):
    c: Tangent(g0,g2) = -1.5708
    c: Tangent(g2,g1) = -1.5708
    c: Tangent(g1,g3) = -1.5708
    c: Tangent(g3,g0) = -1.5708
    c: Coincident(g0,g-1)
    c: PointOnObject(g1,g-1)
    c: DistanceX(g0,g1) = 28.5
    c: Diameter(g0) = 20
    c: Diameter(g1) = 10
FEATURE [PartDesign::Pad] Pad047
  BaseFeature = -> Pad046
  Direction = (0,0,1)
  Length = 8
  Length2 = 10
  Profile = -> Sketch079
  ReferenceAxis = -> Sketch079 [N_Axis]
  Type = 0
FEATURE [Sketcher::SketchObject] Sketch080
  FullyConstrained = true
  MapMode = 5
  Placement = pos=(0,0,30) rot=(0,0,1;0rad)
  Support = -> [Pad047]
  expr: Constraints[1] = <<Dim_table>>.crank_len * 3
  expr: Constraints[2] = <<Dim_table>>.crank_dia1 * 0.25
  sketch-geometry (1):
    g0: Circle CenterX=28.5 CenterY=0 CenterZ=0 NormalX=0 NormalY=0 NormalZ=1 AngleXU=0 Radius=3.125
  constraints (3):
    c: PointOnObject(g0,g-1)
    c: DistanceX(g-1,g0) = 28.5
    c: Diameter(g0) = 6.25
FEATURE [PartDesign::Pad] Pad048
  BaseFeature = -> Pad047
  Direction = (0,0,1)
  Length = 15
  Length2 = 10
  Profile = -> Sketch080
  ReferenceAxis = -> Sketch080 [N_Axis]
  Type = 0
FEATURE [Sketcher::SketchObject] Sketch081
  FullyConstrained = true
  MapMode = 5
  Placement = pos=(0,0,30) rot=(0,0,1;0rad)
  Support = -> [Pad048]
  expr: Constraints[1] = <<Dim_table>>.crank_dia1 * 0.25
  expr: Constraints[3] = <<Dim_table>>.crank_len * 3
  expr: Constraints[4] = <<Dim_table>>.axle_hole_dia
  sketch-geometry (2):
    g0: Circle CenterX=0 CenterY=0 CenterZ=0 NormalX=0 NormalY=0 NormalZ=1 AngleXU=0 Radius=3.125
    g1: Circle CenterX=28.5 CenterY=0 CenterZ=0 NormalX=0 NormalY=0 NormalZ=1 AngleXU=0 Radius=1.5
  constraints (5):
    c: Coincident(g0,g-1)
    c: Diameter(g0) = 6.25
    c: PointOnObject(g1,g-1)
    c: DistanceX(g0,g1) = 28.5
    c: Diameter(g1) = 3
FEATURE [PartDesign::Hole] Hole
  BaseFeature = -> Pad048
  CustomThreadClearance = 0
  Depth = 128.537
  DepthType = 1
  Diameter = 6
  DrillForDepth = false
  DrillPoint = 1
  DrillPointAngle = 118
  HoleCutCountersinkAngle = 90
  HoleCutCustomValues = false
  HoleCutDepth = 0
  HoleCutDiameter = 6.1
  HoleCutType = 0
  ModelThread = false
  Profile = -> Sketch081
  Tapered = false
  TaperedAngle = 90
  ThreadClass = 0
  ThreadDepth = 128.537
  ThreadDepthType = 0
  ThreadDirection = 0
  ThreadFit = 0
  ThreadSize = 0
  ThreadType = 0
  Threaded = false
  UseCustomThreadClearance = false
FEATURE [Sketcher::SketchObject] Sketch082
  FullyConstrained = true
  MapMode = 5
  Placement = pos=(0,0,30) rot=(0,0,1;0rad)
  Support = -> [Hole]
  sketch-geometry (7):
    g0: LineSegment StartX=3.03109 StartY=5.25 StartZ=0 EndX=-3.03109 EndY=5.25 EndZ=0
    g1: LineSegment StartX=-3.03109 StartY=5.25 StartZ=0 EndX=-6.06218 EndY=0 EndZ=0
    g2: LineSegment StartX=-6.06218 StartY=0 StartZ=0 EndX=-3.03109 EndY=-5.25 EndZ=0
    g3: LineSegment StartX=-3.03109 StartY=-5.25 StartZ=0 EndX=3.03109 EndY=-5.25 EndZ=0
    g4: LineSegment StartX=3.03109 StartY=-5.25 StartZ=0 EndX=6.06218 EndY=0 EndZ=0
    g5: LineSegment StartX=6.06218 StartY=0 StartZ=0 EndX=3.03109 EndY=5.25 EndZ=0
    g6: Circle CenterX=0 CenterY=0 CenterZ=0 NormalX=0 NormalY=0 NormalZ=1 AngleXU=0 Radius=6.06218
  constraints (16):
    c: Coincident(g0,g1)
    c: Coincident(g1,g2)
    c: Coincident(g2,g3)
    c: Coincident(g3,g4)
    c: Coincident(g4,g5)
    c: Coincident(g5,g0)
    c: Equal(g0, g1-g5) x5
    c: PointOnObject(g0,g6)
    c: PointOnObject(g1,g6)
    c: PointOnObject(g2,g6)
    c: PointOnObject(g3,g6)
    c: PointOnObject(g4,g6)
    c: PointOnObject(g5,g6)
    c: Coincident(g6,g-1)
    c: Distance(g3,g0) = 10.5
    c: PointOnObject(g1,g-1)
FEATURE [PartDesign::Pocket] Pocket037
  BaseFeature = -> Hole
  Direction = (0,0,-1)
  Length = 5
  Length2 = 5
  Profile = -> Sketch082
  ReferenceAxis = -> Sketch082 [N_Axis]
  Type = 0
FEATURE [PartDesign::Body] Body093  label="ручка"
  Group = -> [Sketch078,Pad046,Sketch079,Pad047,Sketch080,Pad048,Sketch081,Hole,Sketch082,Pocket037]
  Origin = -> Origin097
  Tip = -> Pocket037
